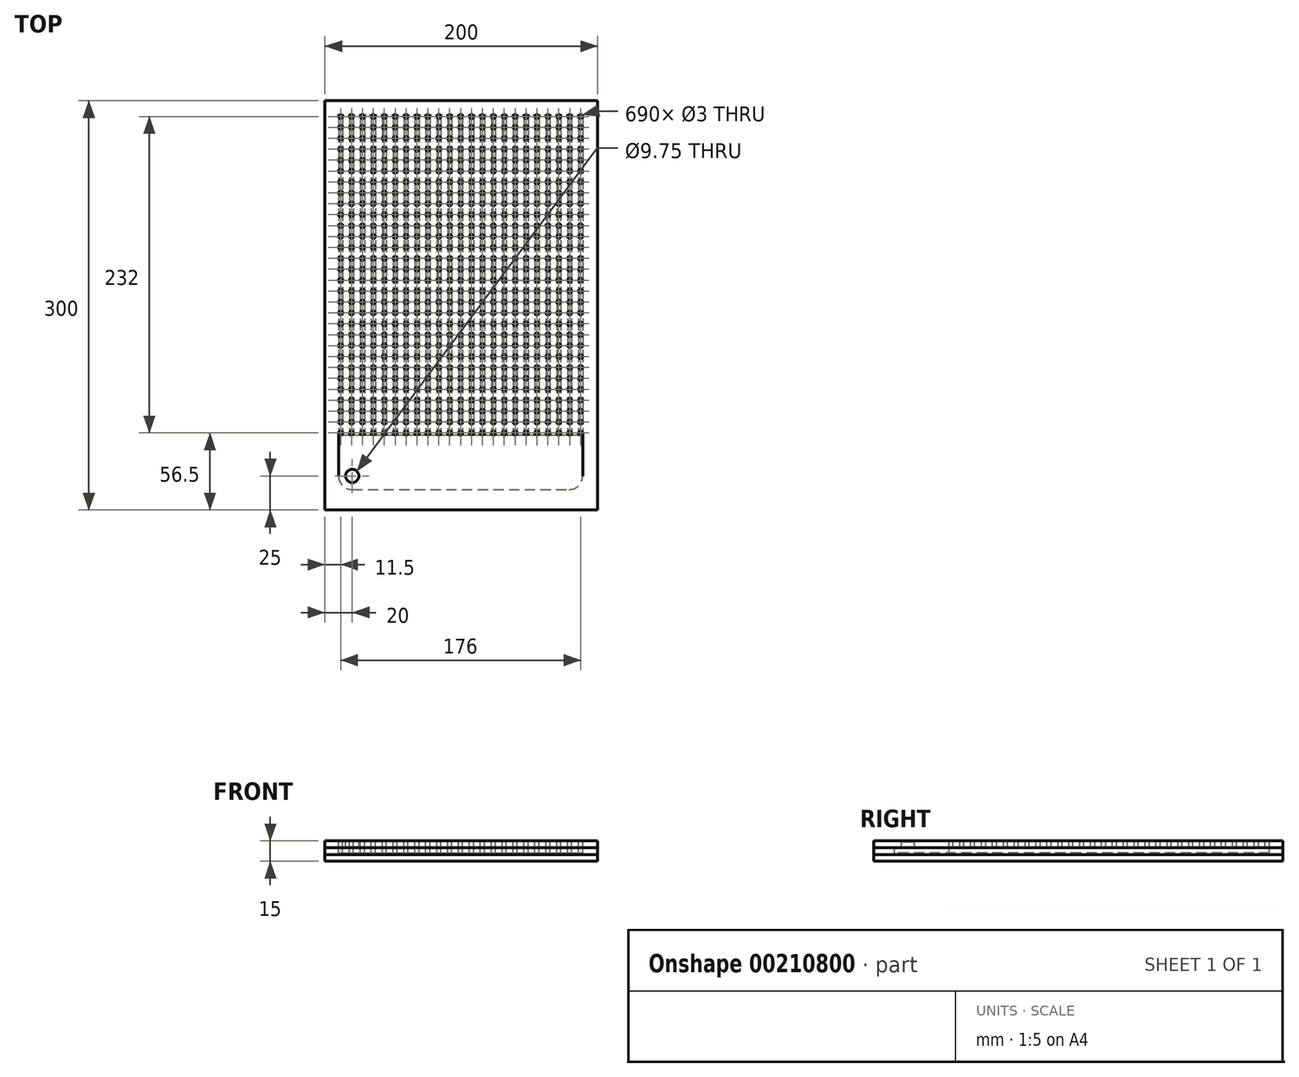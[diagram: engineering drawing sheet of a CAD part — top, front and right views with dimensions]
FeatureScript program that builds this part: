
annotation { "Feature Type Name" : "Feature", "Feature Type Description" : "" }
export const myFeature = defineFeature(function(context is Context, id is Id, definition is map)
    precondition{}
    {
        {
            var Q0;
            Q0=qCreatedBy(makeId("Top.planeOp"),FACE);
            var sketch = newSketch(context, id + "F0", { "sketchPlane" : qUnion([Q0])});
            skLineSegment(sketch, "E0.bottom", {"start": v(0, 0) * mm, "end": v(200, 0) * mm});
            skLineSegment(sketch, "E0.top", {"start": v(0, 300) * mm, "end": v(200, 300) * mm});
            skLineSegment(sketch, "E0.left", {"start": v(0, 0) * mm, "end": v(0, 300) * mm});
            skLineSegment(sketch, "E0.right", {"start": v(200, 0) * mm, "end": v(200, 300) * mm});
            skSolve(sketch);
        }
        {
            var Q0;
            Q0=makeQuery(id+"F0.imprint","IMPRINT",FACE,{"disambiguationData":[TD([[makeQuery(id+"F0.imprint","IMPRINT",EDGE,{"derivedFrom":sQuery(id+"F0.wireOp",EDGE,"E0.bottom")}),1.0]])]});
            extrude(context, id + "F1", {"entities" : qUnion([Q0]), "depth" : 5 * mm});
        }
        {
            var Q0;
            Q0=makeQuery(id+"F1.opExtrude","CAP_FACE",FACE,{"disambiguationData":[OSD([sQuery(id+"F0.wireOp",EDGE,"E0.bottom"),sQuery(id+"F0.wireOp",EDGE,"E0.top"),sQuery(id+"F0.wireOp",EDGE,"E0.left"),sQuery(id+"F0.wireOp",EDGE,"E0.right")])],"isStart":false});
            var sketch = newSketch(context, id + "F2", { "sketchPlane" : qUnion([Q0])});
            skLineSegment(sketch, "E1.0", {"start": v(190, 290) * mm, "end": v(10, 290) * mm, "construction": true});
            skLineSegment(sketch, "E1.1", {"start": v(190, 10) * mm, "end": v(190, 290) * mm, "construction": true});
            skLineSegment(sketch, "E1.2", {"start": v(10, 10) * mm, "end": v(190, 10) * mm, "construction": true});
            skLineSegment(sketch, "E1.3", {"start": v(10, 290) * mm, "end": v(10, 10) * mm, "construction": true});
            skCircle(sketch, "E2", {"center": v(11.5, 288.5) * mm, "radius": 1.5 * mm});
            skCircle(sketch, "E3.0.1.0", {"center": v(11.5, 280.5) * mm, "radius": 1.5 * mm});
            skCircle(sketch, "E3.0.2.0", {"center": v(11.5, 272.5) * mm, "radius": 1.5 * mm});
            skCircle(sketch, "E3.0.3.0", {"center": v(11.5, 264.5) * mm, "radius": 1.5 * mm});
            skCircle(sketch, "E3.0.4.0", {"center": v(11.5, 256.5) * mm, "radius": 1.5 * mm});
            skCircle(sketch, "E3.0.5.0", {"center": v(11.5, 248.5) * mm, "radius": 1.5 * mm});
            skCircle(sketch, "E3.0.6.0", {"center": v(11.5, 240.5) * mm, "radius": 1.5 * mm});
            skCircle(sketch, "E3.0.7.0", {"center": v(11.5, 232.5) * mm, "radius": 1.5 * mm});
            skCircle(sketch, "E3.0.8.0", {"center": v(11.5, 224.5) * mm, "radius": 1.5 * mm});
            skCircle(sketch, "E3.0.9.0", {"center": v(11.5, 216.5) * mm, "radius": 1.5 * mm});
            skCircle(sketch, "E3.0.10.0", {"center": v(11.5, 208.5) * mm, "radius": 1.5 * mm});
            skCircle(sketch, "E3.0.11.0", {"center": v(11.5, 200.5) * mm, "radius": 1.5 * mm});
            skCircle(sketch, "E3.0.12.0", {"center": v(11.5, 192.5) * mm, "radius": 1.5 * mm});
            skCircle(sketch, "E3.0.13.0", {"center": v(11.5, 184.5) * mm, "radius": 1.5 * mm});
            skCircle(sketch, "E3.0.14.0", {"center": v(11.5, 176.5) * mm, "radius": 1.5 * mm});
            skCircle(sketch, "E3.0.15.0", {"center": v(11.5, 168.5) * mm, "radius": 1.5 * mm});
            skCircle(sketch, "E3.0.16.0", {"center": v(11.5, 160.5) * mm, "radius": 1.5 * mm});
            skCircle(sketch, "E3.0.17.0", {"center": v(11.5, 152.5) * mm, "radius": 1.5 * mm});
            skCircle(sketch, "E3.0.18.0", {"center": v(11.5, 144.5) * mm, "radius": 1.5 * mm});
            skCircle(sketch, "E3.0.19.0", {"center": v(11.5, 136.5) * mm, "radius": 1.5 * mm});
            skCircle(sketch, "E3.0.20.0", {"center": v(11.5, 128.5) * mm, "radius": 1.5 * mm});
            skCircle(sketch, "E3.0.21.0", {"center": v(11.5, 120.5) * mm, "radius": 1.5 * mm});
            skCircle(sketch, "E3.0.22.0", {"center": v(11.5, 112.5) * mm, "radius": 1.5 * mm});
            skCircle(sketch, "E3.0.23.0", {"center": v(11.5, 104.5) * mm, "radius": 1.5 * mm});
            skCircle(sketch, "E3.1.0.0", {"center": v(19.5, 288.5) * mm, "radius": 1.5 * mm});
            skCircle(sketch, "E3.1.1.0", {"center": v(19.5, 280.5) * mm, "radius": 1.5 * mm});
            skCircle(sketch, "E3.1.2.0", {"center": v(19.5, 272.5) * mm, "radius": 1.5 * mm});
            skCircle(sketch, "E3.1.3.0", {"center": v(19.5, 264.5) * mm, "radius": 1.5 * mm});
            skCircle(sketch, "E3.1.4.0", {"center": v(19.5, 256.5) * mm, "radius": 1.5 * mm});
            skCircle(sketch, "E3.1.5.0", {"center": v(19.5, 248.5) * mm, "radius": 1.5 * mm});
            skCircle(sketch, "E3.1.6.0", {"center": v(19.5, 240.5) * mm, "radius": 1.5 * mm});
            skCircle(sketch, "E3.1.7.0", {"center": v(19.5, 232.5) * mm, "radius": 1.5 * mm});
            skCircle(sketch, "E3.1.8.0", {"center": v(19.5, 224.5) * mm, "radius": 1.5 * mm});
            skCircle(sketch, "E3.1.9.0", {"center": v(19.5, 216.5) * mm, "radius": 1.5 * mm});
            skCircle(sketch, "E3.1.10.0", {"center": v(19.5, 208.5) * mm, "radius": 1.5 * mm});
            skCircle(sketch, "E3.1.11.0", {"center": v(19.5, 200.5) * mm, "radius": 1.5 * mm});
            skCircle(sketch, "E3.1.12.0", {"center": v(19.5, 192.5) * mm, "radius": 1.5 * mm});
            skCircle(sketch, "E3.1.13.0", {"center": v(19.5, 184.5) * mm, "radius": 1.5 * mm});
            skCircle(sketch, "E3.1.14.0", {"center": v(19.5, 176.5) * mm, "radius": 1.5 * mm});
            skCircle(sketch, "E3.1.15.0", {"center": v(19.5, 168.5) * mm, "radius": 1.5 * mm});
            skCircle(sketch, "E3.1.16.0", {"center": v(19.5, 160.5) * mm, "radius": 1.5 * mm});
            skCircle(sketch, "E3.1.17.0", {"center": v(19.5, 152.5) * mm, "radius": 1.5 * mm});
            skCircle(sketch, "E3.1.18.0", {"center": v(19.5, 144.5) * mm, "radius": 1.5 * mm});
            skCircle(sketch, "E3.1.19.0", {"center": v(19.5, 136.5) * mm, "radius": 1.5 * mm});
            skCircle(sketch, "E3.1.20.0", {"center": v(19.5, 128.5) * mm, "radius": 1.5 * mm});
            skCircle(sketch, "E3.1.21.0", {"center": v(19.5, 120.5) * mm, "radius": 1.5 * mm});
            skCircle(sketch, "E3.1.22.0", {"center": v(19.5, 112.5) * mm, "radius": 1.5 * mm});
            skCircle(sketch, "E3.1.23.0", {"center": v(19.5, 104.5) * mm, "radius": 1.5 * mm});
            skCircle(sketch, "E3.2.0.0", {"center": v(27.5, 288.5) * mm, "radius": 1.5 * mm});
            skCircle(sketch, "E3.2.1.0", {"center": v(27.5, 280.5) * mm, "radius": 1.5 * mm});
            skCircle(sketch, "E3.2.2.0", {"center": v(27.5, 272.5) * mm, "radius": 1.5 * mm});
            skCircle(sketch, "E3.2.3.0", {"center": v(27.5, 264.5) * mm, "radius": 1.5 * mm});
            skCircle(sketch, "E3.2.4.0", {"center": v(27.5, 256.5) * mm, "radius": 1.5 * mm});
            skCircle(sketch, "E3.2.5.0", {"center": v(27.5, 248.5) * mm, "radius": 1.5 * mm});
            skCircle(sketch, "E3.2.6.0", {"center": v(27.5, 240.5) * mm, "radius": 1.5 * mm});
            skCircle(sketch, "E3.2.7.0", {"center": v(27.5, 232.5) * mm, "radius": 1.5 * mm});
            skCircle(sketch, "E3.2.8.0", {"center": v(27.5, 224.5) * mm, "radius": 1.5 * mm});
            skCircle(sketch, "E3.2.9.0", {"center": v(27.5, 216.5) * mm, "radius": 1.5 * mm});
            skCircle(sketch, "E3.2.10.0", {"center": v(27.5, 208.5) * mm, "radius": 1.5 * mm});
            skCircle(sketch, "E3.2.11.0", {"center": v(27.5, 200.5) * mm, "radius": 1.5 * mm});
            skCircle(sketch, "E3.2.12.0", {"center": v(27.5, 192.5) * mm, "radius": 1.5 * mm});
            skCircle(sketch, "E3.2.13.0", {"center": v(27.5, 184.5) * mm, "radius": 1.5 * mm});
            skCircle(sketch, "E3.2.14.0", {"center": v(27.5, 176.5) * mm, "radius": 1.5 * mm});
            skCircle(sketch, "E3.2.15.0", {"center": v(27.5, 168.5) * mm, "radius": 1.5 * mm});
            skCircle(sketch, "E3.2.16.0", {"center": v(27.5, 160.5) * mm, "radius": 1.5 * mm});
            skCircle(sketch, "E3.2.17.0", {"center": v(27.5, 152.5) * mm, "radius": 1.5 * mm});
            skCircle(sketch, "E3.2.18.0", {"center": v(27.5, 144.5) * mm, "radius": 1.5 * mm});
            skCircle(sketch, "E3.2.19.0", {"center": v(27.5, 136.5) * mm, "radius": 1.5 * mm});
            skCircle(sketch, "E3.2.20.0", {"center": v(27.5, 128.5) * mm, "radius": 1.5 * mm});
            skCircle(sketch, "E3.2.21.0", {"center": v(27.5, 120.5) * mm, "radius": 1.5 * mm});
            skCircle(sketch, "E3.2.22.0", {"center": v(27.5, 112.5) * mm, "radius": 1.5 * mm});
            skCircle(sketch, "E3.2.23.0", {"center": v(27.5, 104.5) * mm, "radius": 1.5 * mm});
            skCircle(sketch, "E3.3.0.0", {"center": v(35.5, 288.5) * mm, "radius": 1.5 * mm});
            skCircle(sketch, "E3.3.1.0", {"center": v(35.5, 280.5) * mm, "radius": 1.5 * mm});
            skCircle(sketch, "E3.3.2.0", {"center": v(35.5, 272.5) * mm, "radius": 1.5 * mm});
            skCircle(sketch, "E3.3.3.0", {"center": v(35.5, 264.5) * mm, "radius": 1.5 * mm});
            skCircle(sketch, "E3.3.4.0", {"center": v(35.5, 256.5) * mm, "radius": 1.5 * mm});
            skCircle(sketch, "E3.3.5.0", {"center": v(35.5, 248.5) * mm, "radius": 1.5 * mm});
            skCircle(sketch, "E3.3.6.0", {"center": v(35.5, 240.5) * mm, "radius": 1.5 * mm});
            skCircle(sketch, "E3.3.7.0", {"center": v(35.5, 232.5) * mm, "radius": 1.5 * mm});
            skCircle(sketch, "E3.3.8.0", {"center": v(35.5, 224.5) * mm, "radius": 1.5 * mm});
            skCircle(sketch, "E3.3.9.0", {"center": v(35.5, 216.5) * mm, "radius": 1.5 * mm});
            skCircle(sketch, "E3.3.10.0", {"center": v(35.5, 208.5) * mm, "radius": 1.5 * mm});
            skCircle(sketch, "E3.3.11.0", {"center": v(35.5, 200.5) * mm, "radius": 1.5 * mm});
            skCircle(sketch, "E3.3.12.0", {"center": v(35.5, 192.5) * mm, "radius": 1.5 * mm});
            skCircle(sketch, "E3.3.13.0", {"center": v(35.5, 184.5) * mm, "radius": 1.5 * mm});
            skCircle(sketch, "E3.3.14.0", {"center": v(35.5, 176.5) * mm, "radius": 1.5 * mm});
            skCircle(sketch, "E3.3.15.0", {"center": v(35.5, 168.5) * mm, "radius": 1.5 * mm});
            skCircle(sketch, "E3.3.16.0", {"center": v(35.5, 160.5) * mm, "radius": 1.5 * mm});
            skCircle(sketch, "E3.3.17.0", {"center": v(35.5, 152.5) * mm, "radius": 1.5 * mm});
            skCircle(sketch, "E3.3.18.0", {"center": v(35.5, 144.5) * mm, "radius": 1.5 * mm});
            skCircle(sketch, "E3.3.19.0", {"center": v(35.5, 136.5) * mm, "radius": 1.5 * mm});
            skCircle(sketch, "E3.3.20.0", {"center": v(35.5, 128.5) * mm, "radius": 1.5 * mm});
            skCircle(sketch, "E3.3.21.0", {"center": v(35.5, 120.5) * mm, "radius": 1.5 * mm});
            skCircle(sketch, "E3.3.22.0", {"center": v(35.5, 112.5) * mm, "radius": 1.5 * mm});
            skCircle(sketch, "E3.3.23.0", {"center": v(35.5, 104.5) * mm, "radius": 1.5 * mm});
            skCircle(sketch, "E3.4.0.0", {"center": v(43.5, 288.5) * mm, "radius": 1.5 * mm});
            skCircle(sketch, "E3.4.1.0", {"center": v(43.5, 280.5) * mm, "radius": 1.5 * mm});
            skCircle(sketch, "E3.4.2.0", {"center": v(43.5, 272.5) * mm, "radius": 1.5 * mm});
            skCircle(sketch, "E3.4.3.0", {"center": v(43.5, 264.5) * mm, "radius": 1.5 * mm});
            skCircle(sketch, "E3.4.4.0", {"center": v(43.5, 256.5) * mm, "radius": 1.5 * mm});
            skCircle(sketch, "E3.4.5.0", {"center": v(43.5, 248.5) * mm, "radius": 1.5 * mm});
            skCircle(sketch, "E3.4.6.0", {"center": v(43.5, 240.5) * mm, "radius": 1.5 * mm});
            skCircle(sketch, "E3.4.7.0", {"center": v(43.5, 232.5) * mm, "radius": 1.5 * mm});
            skCircle(sketch, "E3.4.8.0", {"center": v(43.5, 224.5) * mm, "radius": 1.5 * mm});
            skCircle(sketch, "E3.4.9.0", {"center": v(43.5, 216.5) * mm, "radius": 1.5 * mm});
            skCircle(sketch, "E3.4.10.0", {"center": v(43.5, 208.5) * mm, "radius": 1.5 * mm});
            skCircle(sketch, "E3.4.11.0", {"center": v(43.5, 200.5) * mm, "radius": 1.5 * mm});
            skCircle(sketch, "E3.4.12.0", {"center": v(43.5, 192.5) * mm, "radius": 1.5 * mm});
            skCircle(sketch, "E3.4.13.0", {"center": v(43.5, 184.5) * mm, "radius": 1.5 * mm});
            skCircle(sketch, "E3.4.14.0", {"center": v(43.5, 176.5) * mm, "radius": 1.5 * mm});
            skCircle(sketch, "E3.4.15.0", {"center": v(43.5, 168.5) * mm, "radius": 1.5 * mm});
            skCircle(sketch, "E3.4.16.0", {"center": v(43.5, 160.5) * mm, "radius": 1.5 * mm});
            skCircle(sketch, "E3.4.17.0", {"center": v(43.5, 152.5) * mm, "radius": 1.5 * mm});
            skCircle(sketch, "E3.4.18.0", {"center": v(43.5, 144.5) * mm, "radius": 1.5 * mm});
            skCircle(sketch, "E3.4.19.0", {"center": v(43.5, 136.5) * mm, "radius": 1.5 * mm});
            skCircle(sketch, "E3.4.20.0", {"center": v(43.5, 128.5) * mm, "radius": 1.5 * mm});
            skCircle(sketch, "E3.4.21.0", {"center": v(43.5, 120.5) * mm, "radius": 1.5 * mm});
            skCircle(sketch, "E3.4.22.0", {"center": v(43.5, 112.5) * mm, "radius": 1.5 * mm});
            skCircle(sketch, "E3.4.23.0", {"center": v(43.5, 104.5) * mm, "radius": 1.5 * mm});
            skCircle(sketch, "E3.5.0.0", {"center": v(51.5, 288.5) * mm, "radius": 1.5 * mm});
            skCircle(sketch, "E3.5.1.0", {"center": v(51.5, 280.5) * mm, "radius": 1.5 * mm});
            skCircle(sketch, "E3.5.2.0", {"center": v(51.5, 272.5) * mm, "radius": 1.5 * mm});
            skCircle(sketch, "E3.5.3.0", {"center": v(51.5, 264.5) * mm, "radius": 1.5 * mm});
            skCircle(sketch, "E3.5.4.0", {"center": v(51.5, 256.5) * mm, "radius": 1.5 * mm});
            skCircle(sketch, "E3.5.5.0", {"center": v(51.5, 248.5) * mm, "radius": 1.5 * mm});
            skCircle(sketch, "E3.5.6.0", {"center": v(51.5, 240.5) * mm, "radius": 1.5 * mm});
            skCircle(sketch, "E3.5.7.0", {"center": v(51.5, 232.5) * mm, "radius": 1.5 * mm});
            skCircle(sketch, "E3.5.8.0", {"center": v(51.5, 224.5) * mm, "radius": 1.5 * mm});
            skCircle(sketch, "E3.5.9.0", {"center": v(51.5, 216.5) * mm, "radius": 1.5 * mm});
            skCircle(sketch, "E3.5.10.0", {"center": v(51.5, 208.5) * mm, "radius": 1.5 * mm});
            skCircle(sketch, "E3.5.11.0", {"center": v(51.5, 200.5) * mm, "radius": 1.5 * mm});
            skCircle(sketch, "E3.5.12.0", {"center": v(51.5, 192.5) * mm, "radius": 1.5 * mm});
            skCircle(sketch, "E3.5.13.0", {"center": v(51.5, 184.5) * mm, "radius": 1.5 * mm});
            skCircle(sketch, "E3.5.14.0", {"center": v(51.5, 176.5) * mm, "radius": 1.5 * mm});
            skCircle(sketch, "E3.5.15.0", {"center": v(51.5, 168.5) * mm, "radius": 1.5 * mm});
            skCircle(sketch, "E3.5.16.0", {"center": v(51.5, 160.5) * mm, "radius": 1.5 * mm});
            skCircle(sketch, "E3.5.17.0", {"center": v(51.5, 152.5) * mm, "radius": 1.5 * mm});
            skCircle(sketch, "E3.5.18.0", {"center": v(51.5, 144.5) * mm, "radius": 1.5 * mm});
            skCircle(sketch, "E3.5.19.0", {"center": v(51.5, 136.5) * mm, "radius": 1.5 * mm});
            skCircle(sketch, "E3.5.20.0", {"center": v(51.5, 128.5) * mm, "radius": 1.5 * mm});
            skCircle(sketch, "E3.5.21.0", {"center": v(51.5, 120.5) * mm, "radius": 1.5 * mm});
            skCircle(sketch, "E3.5.22.0", {"center": v(51.5, 112.5) * mm, "radius": 1.5 * mm});
            skCircle(sketch, "E3.5.23.0", {"center": v(51.5, 104.5) * mm, "radius": 1.5 * mm});
            skCircle(sketch, "E3.6.0.0", {"center": v(59.5, 288.5) * mm, "radius": 1.5 * mm});
            skCircle(sketch, "E3.6.1.0", {"center": v(59.5, 280.5) * mm, "radius": 1.5 * mm});
            skCircle(sketch, "E3.6.2.0", {"center": v(59.5, 272.5) * mm, "radius": 1.5 * mm});
            skCircle(sketch, "E3.6.3.0", {"center": v(59.5, 264.5) * mm, "radius": 1.5 * mm});
            skCircle(sketch, "E3.6.4.0", {"center": v(59.5, 256.5) * mm, "radius": 1.5 * mm});
            skCircle(sketch, "E3.6.5.0", {"center": v(59.5, 248.5) * mm, "radius": 1.5 * mm});
            skCircle(sketch, "E3.6.6.0", {"center": v(59.5, 240.5) * mm, "radius": 1.5 * mm});
            skCircle(sketch, "E3.6.7.0", {"center": v(59.5, 232.5) * mm, "radius": 1.5 * mm});
            skCircle(sketch, "E3.6.8.0", {"center": v(59.5, 224.5) * mm, "radius": 1.5 * mm});
            skCircle(sketch, "E3.6.9.0", {"center": v(59.5, 216.5) * mm, "radius": 1.5 * mm});
            skCircle(sketch, "E3.6.10.0", {"center": v(59.5, 208.5) * mm, "radius": 1.5 * mm});
            skCircle(sketch, "E3.6.11.0", {"center": v(59.5, 200.5) * mm, "radius": 1.5 * mm});
            skCircle(sketch, "E3.6.12.0", {"center": v(59.5, 192.5) * mm, "radius": 1.5 * mm});
            skCircle(sketch, "E3.6.13.0", {"center": v(59.5, 184.5) * mm, "radius": 1.5 * mm});
            skCircle(sketch, "E3.6.14.0", {"center": v(59.5, 176.5) * mm, "radius": 1.5 * mm});
            skCircle(sketch, "E3.6.15.0", {"center": v(59.5, 168.5) * mm, "radius": 1.5 * mm});
            skCircle(sketch, "E3.6.16.0", {"center": v(59.5, 160.5) * mm, "radius": 1.5 * mm});
            skCircle(sketch, "E3.6.17.0", {"center": v(59.5, 152.5) * mm, "radius": 1.5 * mm});
            skCircle(sketch, "E3.6.18.0", {"center": v(59.5, 144.5) * mm, "radius": 1.5 * mm});
            skCircle(sketch, "E3.6.19.0", {"center": v(59.5, 136.5) * mm, "radius": 1.5 * mm});
            skCircle(sketch, "E3.6.20.0", {"center": v(59.5, 128.5) * mm, "radius": 1.5 * mm});
            skCircle(sketch, "E3.6.21.0", {"center": v(59.5, 120.5) * mm, "radius": 1.5 * mm});
            skCircle(sketch, "E3.6.22.0", {"center": v(59.5, 112.5) * mm, "radius": 1.5 * mm});
            skCircle(sketch, "E3.6.23.0", {"center": v(59.5, 104.5) * mm, "radius": 1.5 * mm});
            skCircle(sketch, "E3.7.0.0", {"center": v(67.5, 288.5) * mm, "radius": 1.5 * mm});
            skCircle(sketch, "E3.7.1.0", {"center": v(67.5, 280.5) * mm, "radius": 1.5 * mm});
            skCircle(sketch, "E3.7.2.0", {"center": v(67.5, 272.5) * mm, "radius": 1.5 * mm});
            skCircle(sketch, "E3.7.3.0", {"center": v(67.5, 264.5) * mm, "radius": 1.5 * mm});
            skCircle(sketch, "E3.7.4.0", {"center": v(67.5, 256.5) * mm, "radius": 1.5 * mm});
            skCircle(sketch, "E3.7.5.0", {"center": v(67.5, 248.5) * mm, "radius": 1.5 * mm});
            skCircle(sketch, "E3.7.6.0", {"center": v(67.5, 240.5) * mm, "radius": 1.5 * mm});
            skCircle(sketch, "E3.7.7.0", {"center": v(67.5, 232.5) * mm, "radius": 1.5 * mm});
            skCircle(sketch, "E3.7.8.0", {"center": v(67.5, 224.5) * mm, "radius": 1.5 * mm});
            skCircle(sketch, "E3.7.9.0", {"center": v(67.5, 216.5) * mm, "radius": 1.5 * mm});
            skCircle(sketch, "E3.7.10.0", {"center": v(67.5, 208.5) * mm, "radius": 1.5 * mm});
            skCircle(sketch, "E3.7.11.0", {"center": v(67.5, 200.5) * mm, "radius": 1.5 * mm});
            skCircle(sketch, "E3.7.12.0", {"center": v(67.5, 192.5) * mm, "radius": 1.5 * mm});
            skCircle(sketch, "E3.7.13.0", {"center": v(67.5, 184.5) * mm, "radius": 1.5 * mm});
            skCircle(sketch, "E3.7.14.0", {"center": v(67.5, 176.5) * mm, "radius": 1.5 * mm});
            skCircle(sketch, "E3.7.15.0", {"center": v(67.5, 168.5) * mm, "radius": 1.5 * mm});
            skCircle(sketch, "E3.7.16.0", {"center": v(67.5, 160.5) * mm, "radius": 1.5 * mm});
            skCircle(sketch, "E3.7.17.0", {"center": v(67.5, 152.5) * mm, "radius": 1.5 * mm});
            skCircle(sketch, "E3.7.18.0", {"center": v(67.5, 144.5) * mm, "radius": 1.5 * mm});
            skCircle(sketch, "E3.7.19.0", {"center": v(67.5, 136.5) * mm, "radius": 1.5 * mm});
            skCircle(sketch, "E3.7.20.0", {"center": v(67.5, 128.5) * mm, "radius": 1.5 * mm});
            skCircle(sketch, "E3.7.21.0", {"center": v(67.5, 120.5) * mm, "radius": 1.5 * mm});
            skCircle(sketch, "E3.7.22.0", {"center": v(67.5, 112.5) * mm, "radius": 1.5 * mm});
            skCircle(sketch, "E3.7.23.0", {"center": v(67.5, 104.5) * mm, "radius": 1.5 * mm});
            skCircle(sketch, "E3.8.0.0", {"center": v(75.5, 288.5) * mm, "radius": 1.5 * mm});
            skCircle(sketch, "E3.8.1.0", {"center": v(75.5, 280.5) * mm, "radius": 1.5 * mm});
            skCircle(sketch, "E3.8.2.0", {"center": v(75.5, 272.5) * mm, "radius": 1.5 * mm});
            skCircle(sketch, "E3.8.3.0", {"center": v(75.5, 264.5) * mm, "radius": 1.5 * mm});
            skCircle(sketch, "E3.8.4.0", {"center": v(75.5, 256.5) * mm, "radius": 1.5 * mm});
            skCircle(sketch, "E3.8.5.0", {"center": v(75.5, 248.5) * mm, "radius": 1.5 * mm});
            skCircle(sketch, "E3.8.6.0", {"center": v(75.5, 240.5) * mm, "radius": 1.5 * mm});
            skCircle(sketch, "E3.8.7.0", {"center": v(75.5, 232.5) * mm, "radius": 1.5 * mm});
            skCircle(sketch, "E3.8.8.0", {"center": v(75.5, 224.5) * mm, "radius": 1.5 * mm});
            skCircle(sketch, "E3.8.9.0", {"center": v(75.5, 216.5) * mm, "radius": 1.5 * mm});
            skCircle(sketch, "E3.8.10.0", {"center": v(75.5, 208.5) * mm, "radius": 1.5 * mm});
            skCircle(sketch, "E3.8.11.0", {"center": v(75.5, 200.5) * mm, "radius": 1.5 * mm});
            skCircle(sketch, "E3.8.12.0", {"center": v(75.5, 192.5) * mm, "radius": 1.5 * mm});
            skCircle(sketch, "E3.8.13.0", {"center": v(75.5, 184.5) * mm, "radius": 1.5 * mm});
            skCircle(sketch, "E3.8.14.0", {"center": v(75.5, 176.5) * mm, "radius": 1.5 * mm});
            skCircle(sketch, "E3.8.15.0", {"center": v(75.5, 168.5) * mm, "radius": 1.5 * mm});
            skCircle(sketch, "E3.8.16.0", {"center": v(75.5, 160.5) * mm, "radius": 1.5 * mm});
            skCircle(sketch, "E3.8.17.0", {"center": v(75.5, 152.5) * mm, "radius": 1.5 * mm});
            skCircle(sketch, "E3.8.18.0", {"center": v(75.5, 144.5) * mm, "radius": 1.5 * mm});
            skCircle(sketch, "E3.8.19.0", {"center": v(75.5, 136.5) * mm, "radius": 1.5 * mm});
            skCircle(sketch, "E3.8.20.0", {"center": v(75.5, 128.5) * mm, "radius": 1.5 * mm});
            skCircle(sketch, "E3.8.21.0", {"center": v(75.5, 120.5) * mm, "radius": 1.5 * mm});
            skCircle(sketch, "E3.8.22.0", {"center": v(75.5, 112.5) * mm, "radius": 1.5 * mm});
            skCircle(sketch, "E3.8.23.0", {"center": v(75.5, 104.5) * mm, "radius": 1.5 * mm});
            skCircle(sketch, "E3.9.0.0", {"center": v(83.5, 288.5) * mm, "radius": 1.5 * mm});
            skCircle(sketch, "E3.9.1.0", {"center": v(83.5, 280.5) * mm, "radius": 1.5 * mm});
            skCircle(sketch, "E3.9.2.0", {"center": v(83.5, 272.5) * mm, "radius": 1.5 * mm});
            skCircle(sketch, "E3.9.3.0", {"center": v(83.5, 264.5) * mm, "radius": 1.5 * mm});
            skCircle(sketch, "E3.9.4.0", {"center": v(83.5, 256.5) * mm, "radius": 1.5 * mm});
            skCircle(sketch, "E3.9.5.0", {"center": v(83.5, 248.5) * mm, "radius": 1.5 * mm});
            skCircle(sketch, "E3.9.6.0", {"center": v(83.5, 240.5) * mm, "radius": 1.5 * mm});
            skCircle(sketch, "E3.9.7.0", {"center": v(83.5, 232.5) * mm, "radius": 1.5 * mm});
            skCircle(sketch, "E3.9.8.0", {"center": v(83.5, 224.5) * mm, "radius": 1.5 * mm});
            skCircle(sketch, "E3.9.9.0", {"center": v(83.5, 216.5) * mm, "radius": 1.5 * mm});
            skCircle(sketch, "E3.9.10.0", {"center": v(83.5, 208.5) * mm, "radius": 1.5 * mm});
            skCircle(sketch, "E3.9.11.0", {"center": v(83.5, 200.5) * mm, "radius": 1.5 * mm});
            skCircle(sketch, "E3.9.12.0", {"center": v(83.5, 192.5) * mm, "radius": 1.5 * mm});
            skCircle(sketch, "E3.9.13.0", {"center": v(83.5, 184.5) * mm, "radius": 1.5 * mm});
            skCircle(sketch, "E3.9.14.0", {"center": v(83.5, 176.5) * mm, "radius": 1.5 * mm});
            skCircle(sketch, "E3.9.15.0", {"center": v(83.5, 168.5) * mm, "radius": 1.5 * mm});
            skCircle(sketch, "E3.9.16.0", {"center": v(83.5, 160.5) * mm, "radius": 1.5 * mm});
            skCircle(sketch, "E3.9.17.0", {"center": v(83.5, 152.5) * mm, "radius": 1.5 * mm});
            skCircle(sketch, "E3.9.18.0", {"center": v(83.5, 144.5) * mm, "radius": 1.5 * mm});
            skCircle(sketch, "E3.9.19.0", {"center": v(83.5, 136.5) * mm, "radius": 1.5 * mm});
            skCircle(sketch, "E3.9.20.0", {"center": v(83.5, 128.5) * mm, "radius": 1.5 * mm});
            skCircle(sketch, "E3.9.21.0", {"center": v(83.5, 120.5) * mm, "radius": 1.5 * mm});
            skCircle(sketch, "E3.9.22.0", {"center": v(83.5, 112.5) * mm, "radius": 1.5 * mm});
            skCircle(sketch, "E3.9.23.0", {"center": v(83.5, 104.5) * mm, "radius": 1.5 * mm});
            skCircle(sketch, "E3.10.0.0", {"center": v(91.5, 288.5) * mm, "radius": 1.5 * mm});
            skCircle(sketch, "E3.10.1.0", {"center": v(91.5, 280.5) * mm, "radius": 1.5 * mm});
            skCircle(sketch, "E3.10.2.0", {"center": v(91.5, 272.5) * mm, "radius": 1.5 * mm});
            skCircle(sketch, "E3.10.3.0", {"center": v(91.5, 264.5) * mm, "radius": 1.5 * mm});
            skCircle(sketch, "E3.10.4.0", {"center": v(91.5, 256.5) * mm, "radius": 1.5 * mm});
            skCircle(sketch, "E3.10.5.0", {"center": v(91.5, 248.5) * mm, "radius": 1.5 * mm});
            skCircle(sketch, "E3.10.6.0", {"center": v(91.5, 240.5) * mm, "radius": 1.5 * mm});
            skCircle(sketch, "E3.10.7.0", {"center": v(91.5, 232.5) * mm, "radius": 1.5 * mm});
            skCircle(sketch, "E3.10.8.0", {"center": v(91.5, 224.5) * mm, "radius": 1.5 * mm});
            skCircle(sketch, "E3.10.9.0", {"center": v(91.5, 216.5) * mm, "radius": 1.5 * mm});
            skCircle(sketch, "E3.10.10.0", {"center": v(91.5, 208.5) * mm, "radius": 1.5 * mm});
            skCircle(sketch, "E3.10.11.0", {"center": v(91.5, 200.5) * mm, "radius": 1.5 * mm});
            skCircle(sketch, "E3.10.12.0", {"center": v(91.5, 192.5) * mm, "radius": 1.5 * mm});
            skCircle(sketch, "E3.10.13.0", {"center": v(91.5, 184.5) * mm, "radius": 1.5 * mm});
            skCircle(sketch, "E3.10.14.0", {"center": v(91.5, 176.5) * mm, "radius": 1.5 * mm});
            skCircle(sketch, "E3.10.15.0", {"center": v(91.5, 168.5) * mm, "radius": 1.5 * mm});
            skCircle(sketch, "E3.10.16.0", {"center": v(91.5, 160.5) * mm, "radius": 1.5 * mm});
            skCircle(sketch, "E3.10.17.0", {"center": v(91.5, 152.5) * mm, "radius": 1.5 * mm});
            skCircle(sketch, "E3.10.18.0", {"center": v(91.5, 144.5) * mm, "radius": 1.5 * mm});
            skCircle(sketch, "E3.10.19.0", {"center": v(91.5, 136.5) * mm, "radius": 1.5 * mm});
            skCircle(sketch, "E3.10.20.0", {"center": v(91.5, 128.5) * mm, "radius": 1.5 * mm});
            skCircle(sketch, "E3.10.21.0", {"center": v(91.5, 120.5) * mm, "radius": 1.5 * mm});
            skCircle(sketch, "E3.10.22.0", {"center": v(91.5, 112.5) * mm, "radius": 1.5 * mm});
            skCircle(sketch, "E3.10.23.0", {"center": v(91.5, 104.5) * mm, "radius": 1.5 * mm});
            skCircle(sketch, "E3.11.0.0", {"center": v(99.5, 288.5) * mm, "radius": 1.5 * mm});
            skCircle(sketch, "E3.11.1.0", {"center": v(99.5, 280.5) * mm, "radius": 1.5 * mm});
            skCircle(sketch, "E3.11.2.0", {"center": v(99.5, 272.5) * mm, "radius": 1.5 * mm});
            skCircle(sketch, "E3.11.3.0", {"center": v(99.5, 264.5) * mm, "radius": 1.5 * mm});
            skCircle(sketch, "E3.11.4.0", {"center": v(99.5, 256.5) * mm, "radius": 1.5 * mm});
            skCircle(sketch, "E3.11.5.0", {"center": v(99.5, 248.5) * mm, "radius": 1.5 * mm});
            skCircle(sketch, "E3.11.6.0", {"center": v(99.5, 240.5) * mm, "radius": 1.5 * mm});
            skCircle(sketch, "E3.11.7.0", {"center": v(99.5, 232.5) * mm, "radius": 1.5 * mm});
            skCircle(sketch, "E3.11.8.0", {"center": v(99.5, 224.5) * mm, "radius": 1.5 * mm});
            skCircle(sketch, "E3.11.9.0", {"center": v(99.5, 216.5) * mm, "radius": 1.5 * mm});
            skCircle(sketch, "E3.11.10.0", {"center": v(99.5, 208.5) * mm, "radius": 1.5 * mm});
            skCircle(sketch, "E3.11.11.0", {"center": v(99.5, 200.5) * mm, "radius": 1.5 * mm});
            skCircle(sketch, "E3.11.12.0", {"center": v(99.5, 192.5) * mm, "radius": 1.5 * mm});
            skCircle(sketch, "E3.11.13.0", {"center": v(99.5, 184.5) * mm, "radius": 1.5 * mm});
            skCircle(sketch, "E3.11.14.0", {"center": v(99.5, 176.5) * mm, "radius": 1.5 * mm});
            skCircle(sketch, "E3.11.15.0", {"center": v(99.5, 168.5) * mm, "radius": 1.5 * mm});
            skCircle(sketch, "E3.11.16.0", {"center": v(99.5, 160.5) * mm, "radius": 1.5 * mm});
            skCircle(sketch, "E3.11.17.0", {"center": v(99.5, 152.5) * mm, "radius": 1.5 * mm});
            skCircle(sketch, "E3.11.18.0", {"center": v(99.5, 144.5) * mm, "radius": 1.5 * mm});
            skCircle(sketch, "E3.11.19.0", {"center": v(99.5, 136.5) * mm, "radius": 1.5 * mm});
            skCircle(sketch, "E3.11.20.0", {"center": v(99.5, 128.5) * mm, "radius": 1.5 * mm});
            skCircle(sketch, "E3.11.21.0", {"center": v(99.5, 120.5) * mm, "radius": 1.5 * mm});
            skCircle(sketch, "E3.11.22.0", {"center": v(99.5, 112.5) * mm, "radius": 1.5 * mm});
            skCircle(sketch, "E3.11.23.0", {"center": v(99.5, 104.5) * mm, "radius": 1.5 * mm});
            skCircle(sketch, "E3.12.0.0", {"center": v(107.5, 288.5) * mm, "radius": 1.5 * mm});
            skCircle(sketch, "E3.12.1.0", {"center": v(107.5, 280.5) * mm, "radius": 1.5 * mm});
            skCircle(sketch, "E3.12.2.0", {"center": v(107.5, 272.5) * mm, "radius": 1.5 * mm});
            skCircle(sketch, "E3.12.3.0", {"center": v(107.5, 264.5) * mm, "radius": 1.5 * mm});
            skCircle(sketch, "E3.12.4.0", {"center": v(107.5, 256.5) * mm, "radius": 1.5 * mm});
            skCircle(sketch, "E3.12.5.0", {"center": v(107.5, 248.5) * mm, "radius": 1.5 * mm});
            skCircle(sketch, "E3.12.6.0", {"center": v(107.5, 240.5) * mm, "radius": 1.5 * mm});
            skCircle(sketch, "E3.12.7.0", {"center": v(107.5, 232.5) * mm, "radius": 1.5 * mm});
            skCircle(sketch, "E3.12.8.0", {"center": v(107.5, 224.5) * mm, "radius": 1.5 * mm});
            skCircle(sketch, "E3.12.9.0", {"center": v(107.5, 216.5) * mm, "radius": 1.5 * mm});
            skCircle(sketch, "E3.12.10.0", {"center": v(107.5, 208.5) * mm, "radius": 1.5 * mm});
            skCircle(sketch, "E3.12.11.0", {"center": v(107.5, 200.5) * mm, "radius": 1.5 * mm});
            skCircle(sketch, "E3.12.12.0", {"center": v(107.5, 192.5) * mm, "radius": 1.5 * mm});
            skCircle(sketch, "E3.12.13.0", {"center": v(107.5, 184.5) * mm, "radius": 1.5 * mm});
            skCircle(sketch, "E3.12.14.0", {"center": v(107.5, 176.5) * mm, "radius": 1.5 * mm});
            skCircle(sketch, "E3.12.15.0", {"center": v(107.5, 168.5) * mm, "radius": 1.5 * mm});
            skCircle(sketch, "E3.12.16.0", {"center": v(107.5, 160.5) * mm, "radius": 1.5 * mm});
            skCircle(sketch, "E3.12.17.0", {"center": v(107.5, 152.5) * mm, "radius": 1.5 * mm});
            skCircle(sketch, "E3.12.18.0", {"center": v(107.5, 144.5) * mm, "radius": 1.5 * mm});
            skCircle(sketch, "E3.12.19.0", {"center": v(107.5, 136.5) * mm, "radius": 1.5 * mm});
            skCircle(sketch, "E3.12.20.0", {"center": v(107.5, 128.5) * mm, "radius": 1.5 * mm});
            skCircle(sketch, "E3.12.21.0", {"center": v(107.5, 120.5) * mm, "radius": 1.5 * mm});
            skCircle(sketch, "E3.12.22.0", {"center": v(107.5, 112.5) * mm, "radius": 1.5 * mm});
            skCircle(sketch, "E3.12.23.0", {"center": v(107.5, 104.5) * mm, "radius": 1.5 * mm});
            skCircle(sketch, "E3.13.0.0", {"center": v(115.5, 288.5) * mm, "radius": 1.5 * mm});
            skCircle(sketch, "E3.13.1.0", {"center": v(115.5, 280.5) * mm, "radius": 1.5 * mm});
            skCircle(sketch, "E3.13.2.0", {"center": v(115.5, 272.5) * mm, "radius": 1.5 * mm});
            skCircle(sketch, "E3.13.3.0", {"center": v(115.5, 264.5) * mm, "radius": 1.5 * mm});
            skCircle(sketch, "E3.13.4.0", {"center": v(115.5, 256.5) * mm, "radius": 1.5 * mm});
            skCircle(sketch, "E3.13.5.0", {"center": v(115.5, 248.5) * mm, "radius": 1.5 * mm});
            skCircle(sketch, "E3.13.6.0", {"center": v(115.5, 240.5) * mm, "radius": 1.5 * mm});
            skCircle(sketch, "E3.13.7.0", {"center": v(115.5, 232.5) * mm, "radius": 1.5 * mm});
            skCircle(sketch, "E3.13.8.0", {"center": v(115.5, 224.5) * mm, "radius": 1.5 * mm});
            skCircle(sketch, "E3.13.9.0", {"center": v(115.5, 216.5) * mm, "radius": 1.5 * mm});
            skCircle(sketch, "E3.13.10.0", {"center": v(115.5, 208.5) * mm, "radius": 1.5 * mm});
            skCircle(sketch, "E3.13.11.0", {"center": v(115.5, 200.5) * mm, "radius": 1.5 * mm});
            skCircle(sketch, "E3.13.12.0", {"center": v(115.5, 192.5) * mm, "radius": 1.5 * mm});
            skCircle(sketch, "E3.13.13.0", {"center": v(115.5, 184.5) * mm, "radius": 1.5 * mm});
            skCircle(sketch, "E3.13.14.0", {"center": v(115.5, 176.5) * mm, "radius": 1.5 * mm});
            skCircle(sketch, "E3.13.15.0", {"center": v(115.5, 168.5) * mm, "radius": 1.5 * mm});
            skCircle(sketch, "E3.13.16.0", {"center": v(115.5, 160.5) * mm, "radius": 1.5 * mm});
            skCircle(sketch, "E3.13.17.0", {"center": v(115.5, 152.5) * mm, "radius": 1.5 * mm});
            skCircle(sketch, "E3.13.18.0", {"center": v(115.5, 144.5) * mm, "radius": 1.5 * mm});
            skCircle(sketch, "E3.13.19.0", {"center": v(115.5, 136.5) * mm, "radius": 1.5 * mm});
            skCircle(sketch, "E3.13.20.0", {"center": v(115.5, 128.5) * mm, "radius": 1.5 * mm});
            skCircle(sketch, "E3.13.21.0", {"center": v(115.5, 120.5) * mm, "radius": 1.5 * mm});
            skCircle(sketch, "E3.13.22.0", {"center": v(115.5, 112.5) * mm, "radius": 1.5 * mm});
            skCircle(sketch, "E3.13.23.0", {"center": v(115.5, 104.5) * mm, "radius": 1.5 * mm});
            skCircle(sketch, "E3.14.0.0", {"center": v(123.5, 288.5) * mm, "radius": 1.5 * mm});
            skCircle(sketch, "E3.14.1.0", {"center": v(123.5, 280.5) * mm, "radius": 1.5 * mm});
            skCircle(sketch, "E3.14.2.0", {"center": v(123.5, 272.5) * mm, "radius": 1.5 * mm});
            skCircle(sketch, "E3.14.3.0", {"center": v(123.5, 264.5) * mm, "radius": 1.5 * mm});
            skCircle(sketch, "E3.14.4.0", {"center": v(123.5, 256.5) * mm, "radius": 1.5 * mm});
            skCircle(sketch, "E3.14.5.0", {"center": v(123.5, 248.5) * mm, "radius": 1.5 * mm});
            skCircle(sketch, "E3.14.6.0", {"center": v(123.5, 240.5) * mm, "radius": 1.5 * mm});
            skCircle(sketch, "E3.14.7.0", {"center": v(123.5, 232.5) * mm, "radius": 1.5 * mm});
            skCircle(sketch, "E3.14.8.0", {"center": v(123.5, 224.5) * mm, "radius": 1.5 * mm});
            skCircle(sketch, "E3.14.9.0", {"center": v(123.5, 216.5) * mm, "radius": 1.5 * mm});
            skCircle(sketch, "E3.14.10.0", {"center": v(123.5, 208.5) * mm, "radius": 1.5 * mm});
            skCircle(sketch, "E3.14.11.0", {"center": v(123.5, 200.5) * mm, "radius": 1.5 * mm});
            skCircle(sketch, "E3.14.12.0", {"center": v(123.5, 192.5) * mm, "radius": 1.5 * mm});
            skCircle(sketch, "E3.14.13.0", {"center": v(123.5, 184.5) * mm, "radius": 1.5 * mm});
            skCircle(sketch, "E3.14.14.0", {"center": v(123.5, 176.5) * mm, "radius": 1.5 * mm});
            skCircle(sketch, "E3.14.15.0", {"center": v(123.5, 168.5) * mm, "radius": 1.5 * mm});
            skCircle(sketch, "E3.14.16.0", {"center": v(123.5, 160.5) * mm, "radius": 1.5 * mm});
            skCircle(sketch, "E3.14.17.0", {"center": v(123.5, 152.5) * mm, "radius": 1.5 * mm});
            skCircle(sketch, "E3.14.18.0", {"center": v(123.5, 144.5) * mm, "radius": 1.5 * mm});
            skCircle(sketch, "E3.14.19.0", {"center": v(123.5, 136.5) * mm, "radius": 1.5 * mm});
            skCircle(sketch, "E3.14.20.0", {"center": v(123.5, 128.5) * mm, "radius": 1.5 * mm});
            skCircle(sketch, "E3.14.21.0", {"center": v(123.5, 120.5) * mm, "radius": 1.5 * mm});
            skCircle(sketch, "E3.14.22.0", {"center": v(123.5, 112.5) * mm, "radius": 1.5 * mm});
            skCircle(sketch, "E3.14.23.0", {"center": v(123.5, 104.5) * mm, "radius": 1.5 * mm});
            skCircle(sketch, "E3.15.0.0", {"center": v(131.5, 288.5) * mm, "radius": 1.5 * mm});
            skCircle(sketch, "E3.15.1.0", {"center": v(131.5, 280.5) * mm, "radius": 1.5 * mm});
            skCircle(sketch, "E3.15.2.0", {"center": v(131.5, 272.5) * mm, "radius": 1.5 * mm});
            skCircle(sketch, "E3.15.3.0", {"center": v(131.5, 264.5) * mm, "radius": 1.5 * mm});
            skCircle(sketch, "E3.15.4.0", {"center": v(131.5, 256.5) * mm, "radius": 1.5 * mm});
            skCircle(sketch, "E3.15.5.0", {"center": v(131.5, 248.5) * mm, "radius": 1.5 * mm});
            skCircle(sketch, "E3.15.6.0", {"center": v(131.5, 240.5) * mm, "radius": 1.5 * mm});
            skCircle(sketch, "E3.15.7.0", {"center": v(131.5, 232.5) * mm, "radius": 1.5 * mm});
            skCircle(sketch, "E3.15.8.0", {"center": v(131.5, 224.5) * mm, "radius": 1.5 * mm});
            skCircle(sketch, "E3.15.9.0", {"center": v(131.5, 216.5) * mm, "radius": 1.5 * mm});
            skCircle(sketch, "E3.15.10.0", {"center": v(131.5, 208.5) * mm, "radius": 1.5 * mm});
            skCircle(sketch, "E3.15.11.0", {"center": v(131.5, 200.5) * mm, "radius": 1.5 * mm});
            skCircle(sketch, "E3.15.12.0", {"center": v(131.5, 192.5) * mm, "radius": 1.5 * mm});
            skCircle(sketch, "E3.15.13.0", {"center": v(131.5, 184.5) * mm, "radius": 1.5 * mm});
            skCircle(sketch, "E3.15.14.0", {"center": v(131.5, 176.5) * mm, "radius": 1.5 * mm});
            skCircle(sketch, "E3.15.15.0", {"center": v(131.5, 168.5) * mm, "radius": 1.5 * mm});
            skCircle(sketch, "E3.15.16.0", {"center": v(131.5, 160.5) * mm, "radius": 1.5 * mm});
            skCircle(sketch, "E3.15.17.0", {"center": v(131.5, 152.5) * mm, "radius": 1.5 * mm});
            skCircle(sketch, "E3.15.18.0", {"center": v(131.5, 144.5) * mm, "radius": 1.5 * mm});
            skCircle(sketch, "E3.15.19.0", {"center": v(131.5, 136.5) * mm, "radius": 1.5 * mm});
            skCircle(sketch, "E3.15.20.0", {"center": v(131.5, 128.5) * mm, "radius": 1.5 * mm});
            skCircle(sketch, "E3.15.21.0", {"center": v(131.5, 120.5) * mm, "radius": 1.5 * mm});
            skCircle(sketch, "E3.15.22.0", {"center": v(131.5, 112.5) * mm, "radius": 1.5 * mm});
            skCircle(sketch, "E3.15.23.0", {"center": v(131.5, 104.5) * mm, "radius": 1.5 * mm});
            skCircle(sketch, "E3.16.0.0", {"center": v(139.5, 288.5) * mm, "radius": 1.5 * mm});
            skCircle(sketch, "E3.16.1.0", {"center": v(139.5, 280.5) * mm, "radius": 1.5 * mm});
            skCircle(sketch, "E3.16.2.0", {"center": v(139.5, 272.5) * mm, "radius": 1.5 * mm});
            skCircle(sketch, "E3.16.3.0", {"center": v(139.5, 264.5) * mm, "radius": 1.5 * mm});
            skCircle(sketch, "E3.16.4.0", {"center": v(139.5, 256.5) * mm, "radius": 1.5 * mm});
            skCircle(sketch, "E3.16.5.0", {"center": v(139.5, 248.5) * mm, "radius": 1.5 * mm});
            skCircle(sketch, "E3.16.6.0", {"center": v(139.5, 240.5) * mm, "radius": 1.5 * mm});
            skCircle(sketch, "E3.16.7.0", {"center": v(139.5, 232.5) * mm, "radius": 1.5 * mm});
            skCircle(sketch, "E3.16.8.0", {"center": v(139.5, 224.5) * mm, "radius": 1.5 * mm});
            skCircle(sketch, "E3.16.9.0", {"center": v(139.5, 216.5) * mm, "radius": 1.5 * mm});
            skCircle(sketch, "E3.16.10.0", {"center": v(139.5, 208.5) * mm, "radius": 1.5 * mm});
            skCircle(sketch, "E3.16.11.0", {"center": v(139.5, 200.5) * mm, "radius": 1.5 * mm});
            skCircle(sketch, "E3.16.12.0", {"center": v(139.5, 192.5) * mm, "radius": 1.5 * mm});
            skCircle(sketch, "E3.16.13.0", {"center": v(139.5, 184.5) * mm, "radius": 1.5 * mm});
            skCircle(sketch, "E3.16.14.0", {"center": v(139.5, 176.5) * mm, "radius": 1.5 * mm});
            skCircle(sketch, "E3.16.15.0", {"center": v(139.5, 168.5) * mm, "radius": 1.5 * mm});
            skCircle(sketch, "E3.16.16.0", {"center": v(139.5, 160.5) * mm, "radius": 1.5 * mm});
            skCircle(sketch, "E3.16.17.0", {"center": v(139.5, 152.5) * mm, "radius": 1.5 * mm});
            skCircle(sketch, "E3.16.18.0", {"center": v(139.5, 144.5) * mm, "radius": 1.5 * mm});
            skCircle(sketch, "E3.16.19.0", {"center": v(139.5, 136.5) * mm, "radius": 1.5 * mm});
            skCircle(sketch, "E3.16.20.0", {"center": v(139.5, 128.5) * mm, "radius": 1.5 * mm});
            skCircle(sketch, "E3.16.21.0", {"center": v(139.5, 120.5) * mm, "radius": 1.5 * mm});
            skCircle(sketch, "E3.16.22.0", {"center": v(139.5, 112.5) * mm, "radius": 1.5 * mm});
            skCircle(sketch, "E3.16.23.0", {"center": v(139.5, 104.5) * mm, "radius": 1.5 * mm});
            skCircle(sketch, "E3.17.0.0", {"center": v(147.5, 288.5) * mm, "radius": 1.5 * mm});
            skCircle(sketch, "E3.17.1.0", {"center": v(147.5, 280.5) * mm, "radius": 1.5 * mm});
            skCircle(sketch, "E3.17.2.0", {"center": v(147.5, 272.5) * mm, "radius": 1.5 * mm});
            skCircle(sketch, "E3.17.3.0", {"center": v(147.5, 264.5) * mm, "radius": 1.5 * mm});
            skCircle(sketch, "E3.17.4.0", {"center": v(147.5, 256.5) * mm, "radius": 1.5 * mm});
            skCircle(sketch, "E3.17.5.0", {"center": v(147.5, 248.5) * mm, "radius": 1.5 * mm});
            skCircle(sketch, "E3.17.6.0", {"center": v(147.5, 240.5) * mm, "radius": 1.5 * mm});
            skCircle(sketch, "E3.17.7.0", {"center": v(147.5, 232.5) * mm, "radius": 1.5 * mm});
            skCircle(sketch, "E3.17.8.0", {"center": v(147.5, 224.5) * mm, "radius": 1.5 * mm});
            skCircle(sketch, "E3.17.9.0", {"center": v(147.5, 216.5) * mm, "radius": 1.5 * mm});
            skCircle(sketch, "E3.17.10.0", {"center": v(147.5, 208.5) * mm, "radius": 1.5 * mm});
            skCircle(sketch, "E3.17.11.0", {"center": v(147.5, 200.5) * mm, "radius": 1.5 * mm});
            skCircle(sketch, "E3.17.12.0", {"center": v(147.5, 192.5) * mm, "radius": 1.5 * mm});
            skCircle(sketch, "E3.17.13.0", {"center": v(147.5, 184.5) * mm, "radius": 1.5 * mm});
            skCircle(sketch, "E3.17.14.0", {"center": v(147.5, 176.5) * mm, "radius": 1.5 * mm});
            skCircle(sketch, "E3.17.15.0", {"center": v(147.5, 168.5) * mm, "radius": 1.5 * mm});
            skCircle(sketch, "E3.17.16.0", {"center": v(147.5, 160.5) * mm, "radius": 1.5 * mm});
            skCircle(sketch, "E3.17.17.0", {"center": v(147.5, 152.5) * mm, "radius": 1.5 * mm});
            skCircle(sketch, "E3.17.18.0", {"center": v(147.5, 144.5) * mm, "radius": 1.5 * mm});
            skCircle(sketch, "E3.17.19.0", {"center": v(147.5, 136.5) * mm, "radius": 1.5 * mm});
            skCircle(sketch, "E3.17.20.0", {"center": v(147.5, 128.5) * mm, "radius": 1.5 * mm});
            skCircle(sketch, "E3.17.21.0", {"center": v(147.5, 120.5) * mm, "radius": 1.5 * mm});
            skCircle(sketch, "E3.17.22.0", {"center": v(147.5, 112.5) * mm, "radius": 1.5 * mm});
            skCircle(sketch, "E3.17.23.0", {"center": v(147.5, 104.5) * mm, "radius": 1.5 * mm});
            skCircle(sketch, "E3.18.0.0", {"center": v(155.5, 288.5) * mm, "radius": 1.5 * mm});
            skCircle(sketch, "E3.18.1.0", {"center": v(155.5, 280.5) * mm, "radius": 1.5 * mm});
            skCircle(sketch, "E3.18.2.0", {"center": v(155.5, 272.5) * mm, "radius": 1.5 * mm});
            skCircle(sketch, "E3.18.3.0", {"center": v(155.5, 264.5) * mm, "radius": 1.5 * mm});
            skCircle(sketch, "E3.18.4.0", {"center": v(155.5, 256.5) * mm, "radius": 1.5 * mm});
            skCircle(sketch, "E3.18.5.0", {"center": v(155.5, 248.5) * mm, "radius": 1.5 * mm});
            skCircle(sketch, "E3.18.6.0", {"center": v(155.5, 240.5) * mm, "radius": 1.5 * mm});
            skCircle(sketch, "E3.18.7.0", {"center": v(155.5, 232.5) * mm, "radius": 1.5 * mm});
            skCircle(sketch, "E3.18.8.0", {"center": v(155.5, 224.5) * mm, "radius": 1.5 * mm});
            skCircle(sketch, "E3.18.9.0", {"center": v(155.5, 216.5) * mm, "radius": 1.5 * mm});
            skCircle(sketch, "E3.18.10.0", {"center": v(155.5, 208.5) * mm, "radius": 1.5 * mm});
            skCircle(sketch, "E3.18.11.0", {"center": v(155.5, 200.5) * mm, "radius": 1.5 * mm});
            skCircle(sketch, "E3.18.12.0", {"center": v(155.5, 192.5) * mm, "radius": 1.5 * mm});
            skCircle(sketch, "E3.18.13.0", {"center": v(155.5, 184.5) * mm, "radius": 1.5 * mm});
            skCircle(sketch, "E3.18.14.0", {"center": v(155.5, 176.5) * mm, "radius": 1.5 * mm});
            skCircle(sketch, "E3.18.15.0", {"center": v(155.5, 168.5) * mm, "radius": 1.5 * mm});
            skCircle(sketch, "E3.18.16.0", {"center": v(155.5, 160.5) * mm, "radius": 1.5 * mm});
            skCircle(sketch, "E3.18.17.0", {"center": v(155.5, 152.5) * mm, "radius": 1.5 * mm});
            skCircle(sketch, "E3.18.18.0", {"center": v(155.5, 144.5) * mm, "radius": 1.5 * mm});
            skCircle(sketch, "E3.18.19.0", {"center": v(155.5, 136.5) * mm, "radius": 1.5 * mm});
            skCircle(sketch, "E3.18.20.0", {"center": v(155.5, 128.5) * mm, "radius": 1.5 * mm});
            skCircle(sketch, "E3.18.21.0", {"center": v(155.5, 120.5) * mm, "radius": 1.5 * mm});
            skCircle(sketch, "E3.18.22.0", {"center": v(155.5, 112.5) * mm, "radius": 1.5 * mm});
            skCircle(sketch, "E3.18.23.0", {"center": v(155.5, 104.5) * mm, "radius": 1.5 * mm});
            skCircle(sketch, "E3.19.0.0", {"center": v(163.5, 288.5) * mm, "radius": 1.5 * mm});
            skCircle(sketch, "E3.19.1.0", {"center": v(163.5, 280.5) * mm, "radius": 1.5 * mm});
            skCircle(sketch, "E3.19.2.0", {"center": v(163.5, 272.5) * mm, "radius": 1.5 * mm});
            skCircle(sketch, "E3.19.3.0", {"center": v(163.5, 264.5) * mm, "radius": 1.5 * mm});
            skCircle(sketch, "E3.19.4.0", {"center": v(163.5, 256.5) * mm, "radius": 1.5 * mm});
            skCircle(sketch, "E3.19.5.0", {"center": v(163.5, 248.5) * mm, "radius": 1.5 * mm});
            skCircle(sketch, "E3.19.6.0", {"center": v(163.5, 240.5) * mm, "radius": 1.5 * mm});
            skCircle(sketch, "E3.19.7.0", {"center": v(163.5, 232.5) * mm, "radius": 1.5 * mm});
            skCircle(sketch, "E3.19.8.0", {"center": v(163.5, 224.5) * mm, "radius": 1.5 * mm});
            skCircle(sketch, "E3.19.9.0", {"center": v(163.5, 216.5) * mm, "radius": 1.5 * mm});
            skCircle(sketch, "E3.19.10.0", {"center": v(163.5, 208.5) * mm, "radius": 1.5 * mm});
            skCircle(sketch, "E3.19.11.0", {"center": v(163.5, 200.5) * mm, "radius": 1.5 * mm});
            skCircle(sketch, "E3.19.12.0", {"center": v(163.5, 192.5) * mm, "radius": 1.5 * mm});
            skCircle(sketch, "E3.19.13.0", {"center": v(163.5, 184.5) * mm, "radius": 1.5 * mm});
            skCircle(sketch, "E3.19.14.0", {"center": v(163.5, 176.5) * mm, "radius": 1.5 * mm});
            skCircle(sketch, "E3.19.15.0", {"center": v(163.5, 168.5) * mm, "radius": 1.5 * mm});
            skCircle(sketch, "E3.19.16.0", {"center": v(163.5, 160.5) * mm, "radius": 1.5 * mm});
            skCircle(sketch, "E3.19.17.0", {"center": v(163.5, 152.5) * mm, "radius": 1.5 * mm});
            skCircle(sketch, "E3.19.18.0", {"center": v(163.5, 144.5) * mm, "radius": 1.5 * mm});
            skCircle(sketch, "E3.19.19.0", {"center": v(163.5, 136.5) * mm, "radius": 1.5 * mm});
            skCircle(sketch, "E3.19.20.0", {"center": v(163.5, 128.5) * mm, "radius": 1.5 * mm});
            skCircle(sketch, "E3.19.21.0", {"center": v(163.5, 120.5) * mm, "radius": 1.5 * mm});
            skCircle(sketch, "E3.19.22.0", {"center": v(163.5, 112.5) * mm, "radius": 1.5 * mm});
            skCircle(sketch, "E3.19.23.0", {"center": v(163.5, 104.5) * mm, "radius": 1.5 * mm});
            skCircle(sketch, "E3.20.0.0", {"center": v(171.5, 288.5) * mm, "radius": 1.5 * mm});
            skCircle(sketch, "E3.20.1.0", {"center": v(171.5, 280.5) * mm, "radius": 1.5 * mm});
            skCircle(sketch, "E3.20.2.0", {"center": v(171.5, 272.5) * mm, "radius": 1.5 * mm});
            skCircle(sketch, "E3.20.3.0", {"center": v(171.5, 264.5) * mm, "radius": 1.5 * mm});
            skCircle(sketch, "E3.20.4.0", {"center": v(171.5, 256.5) * mm, "radius": 1.5 * mm});
            skCircle(sketch, "E3.20.5.0", {"center": v(171.5, 248.5) * mm, "radius": 1.5 * mm});
            skCircle(sketch, "E3.20.6.0", {"center": v(171.5, 240.5) * mm, "radius": 1.5 * mm});
            skCircle(sketch, "E3.20.7.0", {"center": v(171.5, 232.5) * mm, "radius": 1.5 * mm});
            skCircle(sketch, "E3.20.8.0", {"center": v(171.5, 224.5) * mm, "radius": 1.5 * mm});
            skCircle(sketch, "E3.20.9.0", {"center": v(171.5, 216.5) * mm, "radius": 1.5 * mm});
            skCircle(sketch, "E3.20.10.0", {"center": v(171.5, 208.5) * mm, "radius": 1.5 * mm});
            skCircle(sketch, "E3.20.11.0", {"center": v(171.5, 200.5) * mm, "radius": 1.5 * mm});
            skCircle(sketch, "E3.20.12.0", {"center": v(171.5, 192.5) * mm, "radius": 1.5 * mm});
            skCircle(sketch, "E3.20.13.0", {"center": v(171.5, 184.5) * mm, "radius": 1.5 * mm});
            skCircle(sketch, "E3.20.14.0", {"center": v(171.5, 176.5) * mm, "radius": 1.5 * mm});
            skCircle(sketch, "E3.20.15.0", {"center": v(171.5, 168.5) * mm, "radius": 1.5 * mm});
            skCircle(sketch, "E3.20.16.0", {"center": v(171.5, 160.5) * mm, "radius": 1.5 * mm});
            skCircle(sketch, "E3.20.17.0", {"center": v(171.5, 152.5) * mm, "radius": 1.5 * mm});
            skCircle(sketch, "E3.20.18.0", {"center": v(171.5, 144.5) * mm, "radius": 1.5 * mm});
            skCircle(sketch, "E3.20.19.0", {"center": v(171.5, 136.5) * mm, "radius": 1.5 * mm});
            skCircle(sketch, "E3.20.20.0", {"center": v(171.5, 128.5) * mm, "radius": 1.5 * mm});
            skCircle(sketch, "E3.20.21.0", {"center": v(171.5, 120.5) * mm, "radius": 1.5 * mm});
            skCircle(sketch, "E3.20.22.0", {"center": v(171.5, 112.5) * mm, "radius": 1.5 * mm});
            skCircle(sketch, "E3.20.23.0", {"center": v(171.5, 104.5) * mm, "radius": 1.5 * mm});
            skCircle(sketch, "E3.21.0.0", {"center": v(179.5, 288.5) * mm, "radius": 1.5 * mm});
            skCircle(sketch, "E3.21.1.0", {"center": v(179.5, 280.5) * mm, "radius": 1.5 * mm});
            skCircle(sketch, "E3.21.2.0", {"center": v(179.5, 272.5) * mm, "radius": 1.5 * mm});
            skCircle(sketch, "E3.21.3.0", {"center": v(179.5, 264.5) * mm, "radius": 1.5 * mm});
            skCircle(sketch, "E3.21.4.0", {"center": v(179.5, 256.5) * mm, "radius": 1.5 * mm});
            skCircle(sketch, "E3.21.5.0", {"center": v(179.5, 248.5) * mm, "radius": 1.5 * mm});
            skCircle(sketch, "E3.21.6.0", {"center": v(179.5, 240.5) * mm, "radius": 1.5 * mm});
            skCircle(sketch, "E3.21.7.0", {"center": v(179.5, 232.5) * mm, "radius": 1.5 * mm});
            skCircle(sketch, "E3.21.8.0", {"center": v(179.5, 224.5) * mm, "radius": 1.5 * mm});
            skCircle(sketch, "E3.21.9.0", {"center": v(179.5, 216.5) * mm, "radius": 1.5 * mm});
            skCircle(sketch, "E3.21.10.0", {"center": v(179.5, 208.5) * mm, "radius": 1.5 * mm});
            skCircle(sketch, "E3.21.11.0", {"center": v(179.5, 200.5) * mm, "radius": 1.5 * mm});
            skCircle(sketch, "E3.21.12.0", {"center": v(179.5, 192.5) * mm, "radius": 1.5 * mm});
            skCircle(sketch, "E3.21.13.0", {"center": v(179.5, 184.5) * mm, "radius": 1.5 * mm});
            skCircle(sketch, "E3.21.14.0", {"center": v(179.5, 176.5) * mm, "radius": 1.5 * mm});
            skCircle(sketch, "E3.21.15.0", {"center": v(179.5, 168.5) * mm, "radius": 1.5 * mm});
            skCircle(sketch, "E3.21.16.0", {"center": v(179.5, 160.5) * mm, "radius": 1.5 * mm});
            skCircle(sketch, "E3.21.17.0", {"center": v(179.5, 152.5) * mm, "radius": 1.5 * mm});
            skCircle(sketch, "E3.21.18.0", {"center": v(179.5, 144.5) * mm, "radius": 1.5 * mm});
            skCircle(sketch, "E3.21.19.0", {"center": v(179.5, 136.5) * mm, "radius": 1.5 * mm});
            skCircle(sketch, "E3.21.20.0", {"center": v(179.5, 128.5) * mm, "radius": 1.5 * mm});
            skCircle(sketch, "E3.21.21.0", {"center": v(179.5, 120.5) * mm, "radius": 1.5 * mm});
            skCircle(sketch, "E3.21.22.0", {"center": v(179.5, 112.5) * mm, "radius": 1.5 * mm});
            skCircle(sketch, "E3.21.23.0", {"center": v(179.5, 104.5) * mm, "radius": 1.5 * mm});
            skCircle(sketch, "E3.22.0.0", {"center": v(187.5, 288.5) * mm, "radius": 1.5 * mm});
            skCircle(sketch, "E3.22.1.0", {"center": v(187.5, 280.5) * mm, "radius": 1.5 * mm});
            skCircle(sketch, "E3.22.2.0", {"center": v(187.5, 272.5) * mm, "radius": 1.5 * mm});
            skCircle(sketch, "E3.22.3.0", {"center": v(187.5, 264.5) * mm, "radius": 1.5 * mm});
            skCircle(sketch, "E3.22.4.0", {"center": v(187.5, 256.5) * mm, "radius": 1.5 * mm});
            skCircle(sketch, "E3.22.5.0", {"center": v(187.5, 248.5) * mm, "radius": 1.5 * mm});
            skCircle(sketch, "E3.22.6.0", {"center": v(187.5, 240.5) * mm, "radius": 1.5 * mm});
            skCircle(sketch, "E3.22.7.0", {"center": v(187.5, 232.5) * mm, "radius": 1.5 * mm});
            skCircle(sketch, "E3.22.8.0", {"center": v(187.5, 224.5) * mm, "radius": 1.5 * mm});
            skCircle(sketch, "E3.22.9.0", {"center": v(187.5, 216.5) * mm, "radius": 1.5 * mm});
            skCircle(sketch, "E3.22.10.0", {"center": v(187.5, 208.5) * mm, "radius": 1.5 * mm});
            skCircle(sketch, "E3.22.11.0", {"center": v(187.5, 200.5) * mm, "radius": 1.5 * mm});
            skCircle(sketch, "E3.22.12.0", {"center": v(187.5, 192.5) * mm, "radius": 1.5 * mm});
            skCircle(sketch, "E3.22.13.0", {"center": v(187.5, 184.5) * mm, "radius": 1.5 * mm});
            skCircle(sketch, "E3.22.14.0", {"center": v(187.5, 176.5) * mm, "radius": 1.5 * mm});
            skCircle(sketch, "E3.22.15.0", {"center": v(187.5, 168.5) * mm, "radius": 1.5 * mm});
            skCircle(sketch, "E3.22.16.0", {"center": v(187.5, 160.5) * mm, "radius": 1.5 * mm});
            skCircle(sketch, "E3.22.17.0", {"center": v(187.5, 152.5) * mm, "radius": 1.5 * mm});
            skCircle(sketch, "E3.22.18.0", {"center": v(187.5, 144.5) * mm, "radius": 1.5 * mm});
            skCircle(sketch, "E3.22.19.0", {"center": v(187.5, 136.5) * mm, "radius": 1.5 * mm});
            skCircle(sketch, "E3.22.20.0", {"center": v(187.5, 128.5) * mm, "radius": 1.5 * mm});
            skCircle(sketch, "E3.22.21.0", {"center": v(187.5, 120.5) * mm, "radius": 1.5 * mm});
            skCircle(sketch, "E3.22.22.0", {"center": v(187.5, 112.5) * mm, "radius": 1.5 * mm});
            skCircle(sketch, "E3.22.23.0", {"center": v(187.5, 104.5) * mm, "radius": 1.5 * mm});
            skLineSegment(sketch, "E3.direction1", {"start": v(11.5, 288.5) * mm, "end": v(19.5, 288.5) * mm, "construction": true});
            skLineSegment(sketch, "E3.direction2", {"start": v(11.5, 288.5) * mm, "end": v(11.5, 280.5) * mm, "construction": true});
            skCircle(sketch, "E4.0.0.24", {"center": v(11.5, 96.5) * mm, "radius": 1.5 * mm});
            skCircle(sketch, "E4.0.0.25", {"center": v(11.5, 88.5) * mm, "radius": 1.5 * mm});
            skCircle(sketch, "E4.0.0.26", {"center": v(11.5, 80.5) * mm, "radius": 1.5 * mm});
            skCircle(sketch, "E4.0.0.27", {"center": v(11.5, 72.5) * mm, "radius": 1.5 * mm});
            skCircle(sketch, "E4.0.0.28", {"center": v(11.5, 64.5) * mm, "radius": 1.5 * mm});
            skCircle(sketch, "E4.0.0.29", {"center": v(11.5, 56.5) * mm, "radius": 1.5 * mm});
            skCircle(sketch, "E4.0.1.24", {"center": v(19.5, 96.5) * mm, "radius": 1.5 * mm});
            skCircle(sketch, "E4.0.1.25", {"center": v(19.5, 88.5) * mm, "radius": 1.5 * mm});
            skCircle(sketch, "E4.0.1.26", {"center": v(19.5, 80.5) * mm, "radius": 1.5 * mm});
            skCircle(sketch, "E4.0.1.27", {"center": v(19.5, 72.5) * mm, "radius": 1.5 * mm});
            skCircle(sketch, "E4.0.1.28", {"center": v(19.5, 64.5) * mm, "radius": 1.5 * mm});
            skCircle(sketch, "E4.0.1.29", {"center": v(19.5, 56.5) * mm, "radius": 1.5 * mm});
            skCircle(sketch, "E4.0.2.24", {"center": v(27.5, 96.5) * mm, "radius": 1.5 * mm});
            skCircle(sketch, "E4.0.2.25", {"center": v(27.5, 88.5) * mm, "radius": 1.5 * mm});
            skCircle(sketch, "E4.0.2.26", {"center": v(27.5, 80.5) * mm, "radius": 1.5 * mm});
            skCircle(sketch, "E4.0.2.27", {"center": v(27.5, 72.5) * mm, "radius": 1.5 * mm});
            skCircle(sketch, "E4.0.2.28", {"center": v(27.5, 64.5) * mm, "radius": 1.5 * mm});
            skCircle(sketch, "E4.0.2.29", {"center": v(27.5, 56.5) * mm, "radius": 1.5 * mm});
            skCircle(sketch, "E4.0.3.24", {"center": v(35.5, 96.5) * mm, "radius": 1.5 * mm});
            skCircle(sketch, "E4.0.3.25", {"center": v(35.5, 88.5) * mm, "radius": 1.5 * mm});
            skCircle(sketch, "E4.0.3.26", {"center": v(35.5, 80.5) * mm, "radius": 1.5 * mm});
            skCircle(sketch, "E4.0.3.27", {"center": v(35.5, 72.5) * mm, "radius": 1.5 * mm});
            skCircle(sketch, "E4.0.3.28", {"center": v(35.5, 64.5) * mm, "radius": 1.5 * mm});
            skCircle(sketch, "E4.0.3.29", {"center": v(35.5, 56.5) * mm, "radius": 1.5 * mm});
            skCircle(sketch, "E4.0.4.24", {"center": v(43.5, 96.5) * mm, "radius": 1.5 * mm});
            skCircle(sketch, "E4.0.4.25", {"center": v(43.5, 88.5) * mm, "radius": 1.5 * mm});
            skCircle(sketch, "E4.0.4.26", {"center": v(43.5, 80.5) * mm, "radius": 1.5 * mm});
            skCircle(sketch, "E4.0.4.27", {"center": v(43.5, 72.5) * mm, "radius": 1.5 * mm});
            skCircle(sketch, "E4.0.4.28", {"center": v(43.5, 64.5) * mm, "radius": 1.5 * mm});
            skCircle(sketch, "E4.0.4.29", {"center": v(43.5, 56.5) * mm, "radius": 1.5 * mm});
            skCircle(sketch, "E4.0.5.24", {"center": v(51.5, 96.5) * mm, "radius": 1.5 * mm});
            skCircle(sketch, "E4.0.5.25", {"center": v(51.5, 88.5) * mm, "radius": 1.5 * mm});
            skCircle(sketch, "E4.0.5.26", {"center": v(51.5, 80.5) * mm, "radius": 1.5 * mm});
            skCircle(sketch, "E4.0.5.27", {"center": v(51.5, 72.5) * mm, "radius": 1.5 * mm});
            skCircle(sketch, "E4.0.5.28", {"center": v(51.5, 64.5) * mm, "radius": 1.5 * mm});
            skCircle(sketch, "E4.0.5.29", {"center": v(51.5, 56.5) * mm, "radius": 1.5 * mm});
            skCircle(sketch, "E4.0.6.24", {"center": v(59.5, 96.5) * mm, "radius": 1.5 * mm});
            skCircle(sketch, "E4.0.6.25", {"center": v(59.5, 88.5) * mm, "radius": 1.5 * mm});
            skCircle(sketch, "E4.0.6.26", {"center": v(59.5, 80.5) * mm, "radius": 1.5 * mm});
            skCircle(sketch, "E4.0.6.27", {"center": v(59.5, 72.5) * mm, "radius": 1.5 * mm});
            skCircle(sketch, "E4.0.6.28", {"center": v(59.5, 64.5) * mm, "radius": 1.5 * mm});
            skCircle(sketch, "E4.0.6.29", {"center": v(59.5, 56.5) * mm, "radius": 1.5 * mm});
            skCircle(sketch, "E4.0.7.24", {"center": v(67.5, 96.5) * mm, "radius": 1.5 * mm});
            skCircle(sketch, "E4.0.7.25", {"center": v(67.5, 88.5) * mm, "radius": 1.5 * mm});
            skCircle(sketch, "E4.0.7.26", {"center": v(67.5, 80.5) * mm, "radius": 1.5 * mm});
            skCircle(sketch, "E4.0.7.27", {"center": v(67.5, 72.5) * mm, "radius": 1.5 * mm});
            skCircle(sketch, "E4.0.7.28", {"center": v(67.5, 64.5) * mm, "radius": 1.5 * mm});
            skCircle(sketch, "E4.0.7.29", {"center": v(67.5, 56.5) * mm, "radius": 1.5 * mm});
            skCircle(sketch, "E4.0.8.24", {"center": v(75.5, 96.5) * mm, "radius": 1.5 * mm});
            skCircle(sketch, "E4.0.8.25", {"center": v(75.5, 88.5) * mm, "radius": 1.5 * mm});
            skCircle(sketch, "E4.0.8.26", {"center": v(75.5, 80.5) * mm, "radius": 1.5 * mm});
            skCircle(sketch, "E4.0.8.27", {"center": v(75.5, 72.5) * mm, "radius": 1.5 * mm});
            skCircle(sketch, "E4.0.8.28", {"center": v(75.5, 64.5) * mm, "radius": 1.5 * mm});
            skCircle(sketch, "E4.0.8.29", {"center": v(75.5, 56.5) * mm, "radius": 1.5 * mm});
            skCircle(sketch, "E4.0.9.24", {"center": v(83.5, 96.5) * mm, "radius": 1.5 * mm});
            skCircle(sketch, "E4.0.9.25", {"center": v(83.5, 88.5) * mm, "radius": 1.5 * mm});
            skCircle(sketch, "E4.0.9.26", {"center": v(83.5, 80.5) * mm, "radius": 1.5 * mm});
            skCircle(sketch, "E4.0.9.27", {"center": v(83.5, 72.5) * mm, "radius": 1.5 * mm});
            skCircle(sketch, "E4.0.9.28", {"center": v(83.5, 64.5) * mm, "radius": 1.5 * mm});
            skCircle(sketch, "E4.0.9.29", {"center": v(83.5, 56.5) * mm, "radius": 1.5 * mm});
            skCircle(sketch, "E4.0.10.24", {"center": v(91.5, 96.5) * mm, "radius": 1.5 * mm});
            skCircle(sketch, "E4.0.10.25", {"center": v(91.5, 88.5) * mm, "radius": 1.5 * mm});
            skCircle(sketch, "E4.0.10.26", {"center": v(91.5, 80.5) * mm, "radius": 1.5 * mm});
            skCircle(sketch, "E4.0.10.27", {"center": v(91.5, 72.5) * mm, "radius": 1.5 * mm});
            skCircle(sketch, "E4.0.10.28", {"center": v(91.5, 64.5) * mm, "radius": 1.5 * mm});
            skCircle(sketch, "E4.0.10.29", {"center": v(91.5, 56.5) * mm, "radius": 1.5 * mm});
            skCircle(sketch, "E4.0.11.24", {"center": v(99.5, 96.5) * mm, "radius": 1.5 * mm});
            skCircle(sketch, "E4.0.11.25", {"center": v(99.5, 88.5) * mm, "radius": 1.5 * mm});
            skCircle(sketch, "E4.0.11.26", {"center": v(99.5, 80.5) * mm, "radius": 1.5 * mm});
            skCircle(sketch, "E4.0.11.27", {"center": v(99.5, 72.5) * mm, "radius": 1.5 * mm});
            skCircle(sketch, "E4.0.11.28", {"center": v(99.5, 64.5) * mm, "radius": 1.5 * mm});
            skCircle(sketch, "E4.0.11.29", {"center": v(99.5, 56.5) * mm, "radius": 1.5 * mm});
            skCircle(sketch, "E4.0.12.24", {"center": v(107.5, 96.5) * mm, "radius": 1.5 * mm});
            skCircle(sketch, "E4.0.12.25", {"center": v(107.5, 88.5) * mm, "radius": 1.5 * mm});
            skCircle(sketch, "E4.0.12.26", {"center": v(107.5, 80.5) * mm, "radius": 1.5 * mm});
            skCircle(sketch, "E4.0.12.27", {"center": v(107.5, 72.5) * mm, "radius": 1.5 * mm});
            skCircle(sketch, "E4.0.12.28", {"center": v(107.5, 64.5) * mm, "radius": 1.5 * mm});
            skCircle(sketch, "E4.0.12.29", {"center": v(107.5, 56.5) * mm, "radius": 1.5 * mm});
            skCircle(sketch, "E4.0.13.24", {"center": v(115.5, 96.5) * mm, "radius": 1.5 * mm});
            skCircle(sketch, "E4.0.13.25", {"center": v(115.5, 88.5) * mm, "radius": 1.5 * mm});
            skCircle(sketch, "E4.0.13.26", {"center": v(115.5, 80.5) * mm, "radius": 1.5 * mm});
            skCircle(sketch, "E4.0.13.27", {"center": v(115.5, 72.5) * mm, "radius": 1.5 * mm});
            skCircle(sketch, "E4.0.13.28", {"center": v(115.5, 64.5) * mm, "radius": 1.5 * mm});
            skCircle(sketch, "E4.0.13.29", {"center": v(115.5, 56.5) * mm, "radius": 1.5 * mm});
            skCircle(sketch, "E4.0.14.24", {"center": v(123.5, 96.5) * mm, "radius": 1.5 * mm});
            skCircle(sketch, "E4.0.14.25", {"center": v(123.5, 88.5) * mm, "radius": 1.5 * mm});
            skCircle(sketch, "E4.0.14.26", {"center": v(123.5, 80.5) * mm, "radius": 1.5 * mm});
            skCircle(sketch, "E4.0.14.27", {"center": v(123.5, 72.5) * mm, "radius": 1.5 * mm});
            skCircle(sketch, "E4.0.14.28", {"center": v(123.5, 64.5) * mm, "radius": 1.5 * mm});
            skCircle(sketch, "E4.0.14.29", {"center": v(123.5, 56.5) * mm, "radius": 1.5 * mm});
            skCircle(sketch, "E4.0.15.24", {"center": v(131.5, 96.5) * mm, "radius": 1.5 * mm});
            skCircle(sketch, "E4.0.15.25", {"center": v(131.5, 88.5) * mm, "radius": 1.5 * mm});
            skCircle(sketch, "E4.0.15.26", {"center": v(131.5, 80.5) * mm, "radius": 1.5 * mm});
            skCircle(sketch, "E4.0.15.27", {"center": v(131.5, 72.5) * mm, "radius": 1.5 * mm});
            skCircle(sketch, "E4.0.15.28", {"center": v(131.5, 64.5) * mm, "radius": 1.5 * mm});
            skCircle(sketch, "E4.0.15.29", {"center": v(131.5, 56.5) * mm, "radius": 1.5 * mm});
            skCircle(sketch, "E4.0.16.24", {"center": v(139.5, 96.5) * mm, "radius": 1.5 * mm});
            skCircle(sketch, "E4.0.16.25", {"center": v(139.5, 88.5) * mm, "radius": 1.5 * mm});
            skCircle(sketch, "E4.0.16.26", {"center": v(139.5, 80.5) * mm, "radius": 1.5 * mm});
            skCircle(sketch, "E4.0.16.27", {"center": v(139.5, 72.5) * mm, "radius": 1.5 * mm});
            skCircle(sketch, "E4.0.16.28", {"center": v(139.5, 64.5) * mm, "radius": 1.5 * mm});
            skCircle(sketch, "E4.0.16.29", {"center": v(139.5, 56.5) * mm, "radius": 1.5 * mm});
            skCircle(sketch, "E4.0.17.24", {"center": v(147.5, 96.5) * mm, "radius": 1.5 * mm});
            skCircle(sketch, "E4.0.17.25", {"center": v(147.5, 88.5) * mm, "radius": 1.5 * mm});
            skCircle(sketch, "E4.0.17.26", {"center": v(147.5, 80.5) * mm, "radius": 1.5 * mm});
            skCircle(sketch, "E4.0.17.27", {"center": v(147.5, 72.5) * mm, "radius": 1.5 * mm});
            skCircle(sketch, "E4.0.17.28", {"center": v(147.5, 64.5) * mm, "radius": 1.5 * mm});
            skCircle(sketch, "E4.0.17.29", {"center": v(147.5, 56.5) * mm, "radius": 1.5 * mm});
            skCircle(sketch, "E4.0.18.24", {"center": v(155.5, 96.5) * mm, "radius": 1.5 * mm});
            skCircle(sketch, "E4.0.18.25", {"center": v(155.5, 88.5) * mm, "radius": 1.5 * mm});
            skCircle(sketch, "E4.0.18.26", {"center": v(155.5, 80.5) * mm, "radius": 1.5 * mm});
            skCircle(sketch, "E4.0.18.27", {"center": v(155.5, 72.5) * mm, "radius": 1.5 * mm});
            skCircle(sketch, "E4.0.18.28", {"center": v(155.5, 64.5) * mm, "radius": 1.5 * mm});
            skCircle(sketch, "E4.0.18.29", {"center": v(155.5, 56.5) * mm, "radius": 1.5 * mm});
            skCircle(sketch, "E4.0.19.24", {"center": v(163.5, 96.5) * mm, "radius": 1.5 * mm});
            skCircle(sketch, "E4.0.19.25", {"center": v(163.5, 88.5) * mm, "radius": 1.5 * mm});
            skCircle(sketch, "E4.0.19.26", {"center": v(163.5, 80.5) * mm, "radius": 1.5 * mm});
            skCircle(sketch, "E4.0.19.27", {"center": v(163.5, 72.5) * mm, "radius": 1.5 * mm});
            skCircle(sketch, "E4.0.19.28", {"center": v(163.5, 64.5) * mm, "radius": 1.5 * mm});
            skCircle(sketch, "E4.0.19.29", {"center": v(163.5, 56.5) * mm, "radius": 1.5 * mm});
            skCircle(sketch, "E4.0.20.24", {"center": v(171.5, 96.5) * mm, "radius": 1.5 * mm});
            skCircle(sketch, "E4.0.20.25", {"center": v(171.5, 88.5) * mm, "radius": 1.5 * mm});
            skCircle(sketch, "E4.0.20.26", {"center": v(171.5, 80.5) * mm, "radius": 1.5 * mm});
            skCircle(sketch, "E4.0.20.27", {"center": v(171.5, 72.5) * mm, "radius": 1.5 * mm});
            skCircle(sketch, "E4.0.20.28", {"center": v(171.5, 64.5) * mm, "radius": 1.5 * mm});
            skCircle(sketch, "E4.0.20.29", {"center": v(171.5, 56.5) * mm, "radius": 1.5 * mm});
            skCircle(sketch, "E4.0.21.24", {"center": v(179.5, 96.5) * mm, "radius": 1.5 * mm});
            skCircle(sketch, "E4.0.21.25", {"center": v(179.5, 88.5) * mm, "radius": 1.5 * mm});
            skCircle(sketch, "E4.0.21.26", {"center": v(179.5, 80.5) * mm, "radius": 1.5 * mm});
            skCircle(sketch, "E4.0.21.27", {"center": v(179.5, 72.5) * mm, "radius": 1.5 * mm});
            skCircle(sketch, "E4.0.21.28", {"center": v(179.5, 64.5) * mm, "radius": 1.5 * mm});
            skCircle(sketch, "E4.0.21.29", {"center": v(179.5, 56.5) * mm, "radius": 1.5 * mm});
            skCircle(sketch, "E4.0.22.24", {"center": v(187.5, 96.5) * mm, "radius": 1.5 * mm});
            skCircle(sketch, "E4.0.22.25", {"center": v(187.5, 88.5) * mm, "radius": 1.5 * mm});
            skCircle(sketch, "E4.0.22.26", {"center": v(187.5, 80.5) * mm, "radius": 1.5 * mm});
            skCircle(sketch, "E4.0.22.27", {"center": v(187.5, 72.5) * mm, "radius": 1.5 * mm});
            skCircle(sketch, "E4.0.22.28", {"center": v(187.5, 64.5) * mm, "radius": 1.5 * mm});
            skCircle(sketch, "E4.0.22.29", {"center": v(187.5, 56.5) * mm, "radius": 1.5 * mm});
            skSolve(sketch);
        }
        {
            var Q0;
            Q0 = qSketchRegion(id + "F2", true);
            extrude(context, id + "F3", {"entities" : qUnion([Q0]), "operationType" : NewBodyOperationType.REMOVE, "endBound" : BoundingType.THROUGH_ALL, "oppositeDirection" : true, "depth" : 25 * mm});
        }
        {
            var Q0;
            Q0=makeQuery(id+"F1.opExtrude","CAP_FACE",FACE,{"disambiguationData":[OSD([sQuery(id+"F0.wireOp",EDGE,"E0.bottom"),sQuery(id+"F0.wireOp",EDGE,"E0.top"),sQuery(id+"F0.wireOp",EDGE,"E0.left"),sQuery(id+"F0.wireOp",EDGE,"E0.right")])],"isStart":true});
            var sketch = newSketch(context, id + "F4", { "sketchPlane" : qUnion([Q0])});
            skLineSegment(sketch, "E5.0", {"start": v(0, -300) * mm, "end": v(200, -300) * mm});
            skLineSegment(sketch, "E6.0", {"start": v(200, 0) * mm, "end": v(200, -300) * mm});
            skLineSegment(sketch, "E7.0", {"start": v(0, 0) * mm, "end": v(200, 0) * mm});
            skLineSegment(sketch, "E8.0", {"start": v(0, 0) * mm, "end": v(0, -300) * mm});
            skSolve(sketch);
        }
        {
            var Q0;
            Q0 = qSketchRegion(id + "F4", true);
            extrude(context, id + "F5", {"entities" : qUnion([Q0]), "depth" : 5 * mm});
        }
        {
            var Q0;
            Q0=makeQuery(id+"F5.opExtrude","CAP_FACE",FACE,{"disambiguationData":[OSD([sQuery(id+"F4.wireOp",EDGE,"E5.0"),sQuery(id+"F4.wireOp",EDGE,"E6.0"),sQuery(id+"F4.wireOp",EDGE,"E7.0"),sQuery(id+"F4.wireOp",EDGE,"E8.0")])],"isStart":true});
            var sketch = newSketch(context, id + "F6", { "sketchPlane" : qUnion([Q0])});
            skLineSegment(sketch, "E9.0", {"start": v(190, 55) * mm, "end": v(190, 290) * mm, "construction": true});
            skLineSegment(sketch, "E9.1", {"start": v(10, 290) * mm, "end": v(190, 290) * mm, "construction": true});
            skLineSegment(sketch, "E9.2", {"start": v(10, 55) * mm, "end": v(10, 290) * mm, "construction": true});
            skLineSegment(sketch, "E10.bottom", {"start": v(10, 290) * mm, "end": v(13, 290) * mm});
            skLineSegment(sketch, "E10.top", {"start": v(10, 55) * mm, "end": v(13, 55) * mm});
            skLineSegment(sketch, "E10.left", {"start": v(10, 290) * mm, "end": v(10, 55) * mm});
            skLineSegment(sketch, "E10.right", {"start": v(13, 290) * mm, "end": v(13, 55) * mm});
            skLineSegment(sketch, "E11.1.0.0", {"start": v(18, 55) * mm, "end": v(18, 290) * mm, "construction": true});
            skLineSegment(sketch, "E11.1.0.1", {"start": v(21, 290) * mm, "end": v(21, 55) * mm});
            skLineSegment(sketch, "E11.1.0.2", {"start": v(18, 290) * mm, "end": v(18, 55) * mm});
            skLineSegment(sketch, "E11.1.0.3", {"start": v(18, 290) * mm, "end": v(21, 290) * mm});
            skLineSegment(sketch, "E11.1.0.4", {"start": v(18, 55) * mm, "end": v(21, 55) * mm});
            skLineSegment(sketch, "E11.2.0.0", {"start": v(26, 55) * mm, "end": v(26, 290) * mm, "construction": true});
            skLineSegment(sketch, "E11.2.0.1", {"start": v(29, 290) * mm, "end": v(29, 55) * mm});
            skLineSegment(sketch, "E11.2.0.2", {"start": v(26, 290) * mm, "end": v(26, 55) * mm});
            skLineSegment(sketch, "E11.2.0.3", {"start": v(26, 290) * mm, "end": v(29, 290) * mm});
            skLineSegment(sketch, "E11.2.0.4", {"start": v(26, 55) * mm, "end": v(29, 55) * mm});
            skLineSegment(sketch, "E11.3.0.0", {"start": v(34, 55) * mm, "end": v(34, 290) * mm, "construction": true});
            skLineSegment(sketch, "E11.3.0.1", {"start": v(37, 290) * mm, "end": v(37, 55) * mm});
            skLineSegment(sketch, "E11.3.0.2", {"start": v(34, 290) * mm, "end": v(34, 55) * mm});
            skLineSegment(sketch, "E11.3.0.3", {"start": v(34, 290) * mm, "end": v(37, 290) * mm});
            skLineSegment(sketch, "E11.3.0.4", {"start": v(34, 55) * mm, "end": v(37, 55) * mm});
            skLineSegment(sketch, "E11.4.0.0", {"start": v(42, 55) * mm, "end": v(42, 290) * mm, "construction": true});
            skLineSegment(sketch, "E11.4.0.1", {"start": v(45, 290) * mm, "end": v(45, 55) * mm});
            skLineSegment(sketch, "E11.4.0.2", {"start": v(42, 290) * mm, "end": v(42, 55) * mm});
            skLineSegment(sketch, "E11.4.0.3", {"start": v(42, 290) * mm, "end": v(45, 290) * mm});
            skLineSegment(sketch, "E11.4.0.4", {"start": v(42, 55) * mm, "end": v(45, 55) * mm});
            skLineSegment(sketch, "E11.5.0.0", {"start": v(50, 55) * mm, "end": v(50, 290) * mm, "construction": true});
            skLineSegment(sketch, "E11.5.0.1", {"start": v(53, 290) * mm, "end": v(53, 55) * mm});
            skLineSegment(sketch, "E11.5.0.2", {"start": v(50, 290) * mm, "end": v(50, 55) * mm});
            skLineSegment(sketch, "E11.5.0.3", {"start": v(50, 290) * mm, "end": v(53, 290) * mm});
            skLineSegment(sketch, "E11.5.0.4", {"start": v(50, 55) * mm, "end": v(53, 55) * mm});
            skLineSegment(sketch, "E11.6.0.0", {"start": v(58, 55) * mm, "end": v(58, 290) * mm, "construction": true});
            skLineSegment(sketch, "E11.6.0.1", {"start": v(61, 290) * mm, "end": v(61, 55) * mm});
            skLineSegment(sketch, "E11.6.0.2", {"start": v(58, 290) * mm, "end": v(58, 55) * mm});
            skLineSegment(sketch, "E11.6.0.3", {"start": v(58, 290) * mm, "end": v(61, 290) * mm});
            skLineSegment(sketch, "E11.6.0.4", {"start": v(58, 55) * mm, "end": v(61, 55) * mm});
            skLineSegment(sketch, "E11.7.0.0", {"start": v(66, 55) * mm, "end": v(66, 290) * mm, "construction": true});
            skLineSegment(sketch, "E11.7.0.1", {"start": v(69, 290) * mm, "end": v(69, 55) * mm});
            skLineSegment(sketch, "E11.7.0.2", {"start": v(66, 290) * mm, "end": v(66, 55) * mm});
            skLineSegment(sketch, "E11.7.0.3", {"start": v(66, 290) * mm, "end": v(69, 290) * mm});
            skLineSegment(sketch, "E11.7.0.4", {"start": v(66, 55) * mm, "end": v(69, 55) * mm});
            skLineSegment(sketch, "E11.8.0.0", {"start": v(74, 55) * mm, "end": v(74, 290) * mm, "construction": true});
            skLineSegment(sketch, "E11.8.0.1", {"start": v(77, 290) * mm, "end": v(77, 55) * mm});
            skLineSegment(sketch, "E11.8.0.2", {"start": v(74, 290) * mm, "end": v(74, 55) * mm});
            skLineSegment(sketch, "E11.8.0.3", {"start": v(74, 290) * mm, "end": v(77, 290) * mm});
            skLineSegment(sketch, "E11.8.0.4", {"start": v(74, 55) * mm, "end": v(77, 55) * mm});
            skLineSegment(sketch, "E11.9.0.0", {"start": v(82, 55) * mm, "end": v(82, 290) * mm, "construction": true});
            skLineSegment(sketch, "E11.9.0.1", {"start": v(85, 290) * mm, "end": v(85, 55) * mm});
            skLineSegment(sketch, "E11.9.0.2", {"start": v(82, 290) * mm, "end": v(82, 55) * mm});
            skLineSegment(sketch, "E11.9.0.3", {"start": v(82, 290) * mm, "end": v(85, 290) * mm});
            skLineSegment(sketch, "E11.9.0.4", {"start": v(82, 55) * mm, "end": v(85, 55) * mm});
            skLineSegment(sketch, "E11.10.0.0", {"start": v(90, 55) * mm, "end": v(90, 290) * mm, "construction": true});
            skLineSegment(sketch, "E11.10.0.1", {"start": v(93, 290) * mm, "end": v(93, 55) * mm});
            skLineSegment(sketch, "E11.10.0.2", {"start": v(90, 290) * mm, "end": v(90, 55) * mm});
            skLineSegment(sketch, "E11.10.0.3", {"start": v(90, 290) * mm, "end": v(93, 290) * mm});
            skLineSegment(sketch, "E11.10.0.4", {"start": v(90, 55) * mm, "end": v(93, 55) * mm});
            skLineSegment(sketch, "E11.11.0.0", {"start": v(98, 55) * mm, "end": v(98, 290) * mm, "construction": true});
            skLineSegment(sketch, "E11.11.0.1", {"start": v(101, 290) * mm, "end": v(101, 55) * mm});
            skLineSegment(sketch, "E11.11.0.2", {"start": v(98, 290) * mm, "end": v(98, 55) * mm});
            skLineSegment(sketch, "E11.11.0.3", {"start": v(98, 290) * mm, "end": v(101, 290) * mm});
            skLineSegment(sketch, "E11.11.0.4", {"start": v(98, 55) * mm, "end": v(101, 55) * mm});
            skLineSegment(sketch, "E11.12.0.0", {"start": v(106, 55) * mm, "end": v(106, 290) * mm, "construction": true});
            skLineSegment(sketch, "E11.12.0.1", {"start": v(109, 290) * mm, "end": v(109, 55) * mm});
            skLineSegment(sketch, "E11.12.0.2", {"start": v(106, 290) * mm, "end": v(106, 55) * mm});
            skLineSegment(sketch, "E11.12.0.3", {"start": v(106, 290) * mm, "end": v(109, 290) * mm});
            skLineSegment(sketch, "E11.12.0.4", {"start": v(106, 55) * mm, "end": v(109, 55) * mm});
            skLineSegment(sketch, "E11.13.0.0", {"start": v(114, 55) * mm, "end": v(114, 290) * mm, "construction": true});
            skLineSegment(sketch, "E11.13.0.1", {"start": v(117, 290) * mm, "end": v(117, 55) * mm});
            skLineSegment(sketch, "E11.13.0.2", {"start": v(114, 290) * mm, "end": v(114, 55) * mm});
            skLineSegment(sketch, "E11.13.0.3", {"start": v(114, 290) * mm, "end": v(117, 290) * mm});
            skLineSegment(sketch, "E11.13.0.4", {"start": v(114, 55) * mm, "end": v(117, 55) * mm});
            skLineSegment(sketch, "E11.14.0.0", {"start": v(122, 55) * mm, "end": v(122, 290) * mm, "construction": true});
            skLineSegment(sketch, "E11.14.0.1", {"start": v(125, 290) * mm, "end": v(125, 55) * mm});
            skLineSegment(sketch, "E11.14.0.2", {"start": v(122, 290) * mm, "end": v(122, 55) * mm});
            skLineSegment(sketch, "E11.14.0.3", {"start": v(122, 290) * mm, "end": v(125, 290) * mm});
            skLineSegment(sketch, "E11.14.0.4", {"start": v(122, 55) * mm, "end": v(125, 55) * mm});
            skLineSegment(sketch, "E11.15.0.0", {"start": v(130, 55) * mm, "end": v(130, 290) * mm, "construction": true});
            skLineSegment(sketch, "E11.15.0.1", {"start": v(133, 290) * mm, "end": v(133, 55) * mm});
            skLineSegment(sketch, "E11.15.0.2", {"start": v(130, 290) * mm, "end": v(130, 55) * mm});
            skLineSegment(sketch, "E11.15.0.3", {"start": v(130, 290) * mm, "end": v(133, 290) * mm});
            skLineSegment(sketch, "E11.15.0.4", {"start": v(130, 55) * mm, "end": v(133, 55) * mm});
            skLineSegment(sketch, "E11.16.0.0", {"start": v(138, 55) * mm, "end": v(138, 290) * mm, "construction": true});
            skLineSegment(sketch, "E11.16.0.1", {"start": v(141, 290) * mm, "end": v(141, 55) * mm});
            skLineSegment(sketch, "E11.16.0.2", {"start": v(138, 290) * mm, "end": v(138, 55) * mm});
            skLineSegment(sketch, "E11.16.0.3", {"start": v(138, 290) * mm, "end": v(141, 290) * mm});
            skLineSegment(sketch, "E11.16.0.4", {"start": v(138, 55) * mm, "end": v(141, 55) * mm});
            skLineSegment(sketch, "E11.17.0.0", {"start": v(146, 55) * mm, "end": v(146, 290) * mm, "construction": true});
            skLineSegment(sketch, "E11.17.0.1", {"start": v(149, 290) * mm, "end": v(149, 55) * mm});
            skLineSegment(sketch, "E11.17.0.2", {"start": v(146, 290) * mm, "end": v(146, 55) * mm});
            skLineSegment(sketch, "E11.17.0.3", {"start": v(146, 290) * mm, "end": v(149, 290) * mm});
            skLineSegment(sketch, "E11.17.0.4", {"start": v(146, 55) * mm, "end": v(149, 55) * mm});
            skLineSegment(sketch, "E11.18.0.0", {"start": v(154, 55) * mm, "end": v(154, 290) * mm, "construction": true});
            skLineSegment(sketch, "E11.18.0.1", {"start": v(157, 290) * mm, "end": v(157, 55) * mm});
            skLineSegment(sketch, "E11.18.0.2", {"start": v(154, 290) * mm, "end": v(154, 55) * mm});
            skLineSegment(sketch, "E11.18.0.3", {"start": v(154, 290) * mm, "end": v(157, 290) * mm});
            skLineSegment(sketch, "E11.18.0.4", {"start": v(154, 55) * mm, "end": v(157, 55) * mm});
            skLineSegment(sketch, "E11.19.0.0", {"start": v(162, 55) * mm, "end": v(162, 290) * mm, "construction": true});
            skLineSegment(sketch, "E11.19.0.1", {"start": v(165, 290) * mm, "end": v(165, 55) * mm});
            skLineSegment(sketch, "E11.19.0.2", {"start": v(162, 290) * mm, "end": v(162, 55) * mm});
            skLineSegment(sketch, "E11.19.0.3", {"start": v(162, 290) * mm, "end": v(165, 290) * mm});
            skLineSegment(sketch, "E11.19.0.4", {"start": v(162, 55) * mm, "end": v(165, 55) * mm});
            skLineSegment(sketch, "E11.20.0.0", {"start": v(170, 55) * mm, "end": v(170, 290) * mm, "construction": true});
            skLineSegment(sketch, "E11.20.0.1", {"start": v(173, 290) * mm, "end": v(173, 55) * mm});
            skLineSegment(sketch, "E11.20.0.2", {"start": v(170, 290) * mm, "end": v(170, 55) * mm});
            skLineSegment(sketch, "E11.20.0.3", {"start": v(170, 290) * mm, "end": v(173, 290) * mm});
            skLineSegment(sketch, "E11.20.0.4", {"start": v(170, 55) * mm, "end": v(173, 55) * mm});
            skLineSegment(sketch, "E11.21.0.0", {"start": v(178, 55) * mm, "end": v(178, 290) * mm, "construction": true});
            skLineSegment(sketch, "E11.21.0.1", {"start": v(181, 290) * mm, "end": v(181, 55) * mm});
            skLineSegment(sketch, "E11.21.0.2", {"start": v(178, 290) * mm, "end": v(178, 55) * mm});
            skLineSegment(sketch, "E11.21.0.3", {"start": v(178, 290) * mm, "end": v(181, 290) * mm});
            skLineSegment(sketch, "E11.21.0.4", {"start": v(178, 55) * mm, "end": v(181, 55) * mm});
            skLineSegment(sketch, "E11.22.0.0", {"start": v(186, 55) * mm, "end": v(186, 290) * mm, "construction": true});
            skLineSegment(sketch, "E11.22.0.1", {"start": v(189, 290) * mm, "end": v(189, 55) * mm});
            skLineSegment(sketch, "E11.22.0.2", {"start": v(186, 290) * mm, "end": v(186, 55) * mm});
            skLineSegment(sketch, "E11.22.0.3", {"start": v(186, 290) * mm, "end": v(189, 290) * mm});
            skLineSegment(sketch, "E11.22.0.4", {"start": v(186, 55) * mm, "end": v(189, 55) * mm});
            skLineSegment(sketch, "E11.direction1", {"start": v(10, 55) * mm, "end": v(18, 55) * mm, "construction": true});
            skLineSegment(sketch, "E12.bottom", {"start": v(10, 55) * mm, "end": v(189, 55) * mm});
            skLineSegment(sketch, "E12.top", {"start": v(20, 15) * mm, "end": v(179, 15) * mm});
            skLineSegment(sketch, "E12.left", {"start": v(10, 55) * mm, "end": v(10, 25) * mm});
            skLineSegment(sketch, "E12.right", {"start": v(189, 55) * mm, "end": v(189, 25) * mm});
            skPoint(sketch, "E13.visualSharp", {"position": v(10, 15) * mm});
            skArc(sketch, "E13.filletArc", {"start": v(10, 25) * mm, "mid": v(12.93, 17.93) * mm, "end": v(20, 15) * mm});
            skPoint(sketch, "E14.visualSharp", {"position": v(189, 15) * mm});
            skArc(sketch, "E14.filletArc", {"start": v(179, 15) * mm, "mid": v(186.07, 17.93) * mm, "end": v(189, 25) * mm});
            skSolve(sketch);
        }
        {
            var Q0;
            Q0 = qSketchRegion(id + "F6", true);
            extrude(context, id + "F7", {"entities" : qUnion([Q0]), "operationType" : NewBodyOperationType.REMOVE, "oppositeDirection" : true, "depth" : 4 * mm});
        }
        {
            var Q0;
            Q0=makeQuery(id+"F1.opExtrude","CAP_FACE",FACE,{"disambiguationData":[OSD([sQuery(id+"F0.wireOp",EDGE,"E0.bottom"),sQuery(id+"F0.wireOp",EDGE,"E0.top"),sQuery(id+"F0.wireOp",EDGE,"E0.left"),sQuery(id+"F0.wireOp",EDGE,"E0.right")])],"isStart":false});
            var sketch = newSketch(context, id + "F8", { "sketchPlane" : qUnion([Q0])});
            skCircle(sketch, "E15", {"center": v(20, 25) * mm, "radius": 4.88 * mm});
            skSolve(sketch);
        }
        {
            var Q0;
            Q0=makeQuery(id+"F8.imprint","IMPRINT",FACE,{"disambiguationData":[TD([[makeQuery(id+"F8.imprint","IMPRINT",EDGE,{"derivedFrom":sQuery(id+"F8.wireOp",EDGE,"E15")}),1.0]])]});
            extrude(context, id + "F9", {"entities" : qUnion([Q0]), "operationType" : NewBodyOperationType.REMOVE, "oppositeDirection" : true, "depth" : 5 * mm});
        }
        {
            var Q0;
            Q0=makeQuery(id+"F5.opExtrude","CAP_FACE",FACE,{"disambiguationData":[OSD([sQuery(id+"F4.wireOp",EDGE,"E5.0"),sQuery(id+"F4.wireOp",EDGE,"E6.0"),sQuery(id+"F4.wireOp",EDGE,"E7.0"),sQuery(id+"F4.wireOp",EDGE,"E8.0")])],"isStart":false});
            extrude(context, id + "F10", {"entities" : qUnion([Q0]), "depth" : 5 * mm});
        }
        {
            var Q0;
            Q0=makeQuery(id+"F1.opExtrude","CAP_FACE",FACE,{"disambiguationData":[OSD([sQuery(id+"F0.wireOp",EDGE,"E0.bottom"),sQuery(id+"F0.wireOp",EDGE,"E0.top"),sQuery(id+"F0.wireOp",EDGE,"E0.left"),sQuery(id+"F0.wireOp",EDGE,"E0.right")])],"isStart":false});
            var sketch = newSketch(context, id + "F11", { "sketchPlane" : qUnion([Q0])});
            skCircle(sketch, "E16.0", {"center": v(20, 25) * mm, "radius": 4.88 * mm});
            skSolve(sketch);
        }
        {
            var Q0;
            Q0=makeQuery(id+"F11.imprint","IMPRINT",FACE,{"disambiguationData":[TD([[makeQuery(id+"F11.imprint","IMPRINT",EDGE,{"derivedFrom":sQuery(id+"F11.wireOp",EDGE,"E16.0")}),1.0]])]});
            extrude(context, id + "F12", {"entities" : qUnion([Q0]), "oppositeDirection" : true, "depth" : .5 * mm});
        }
    });
